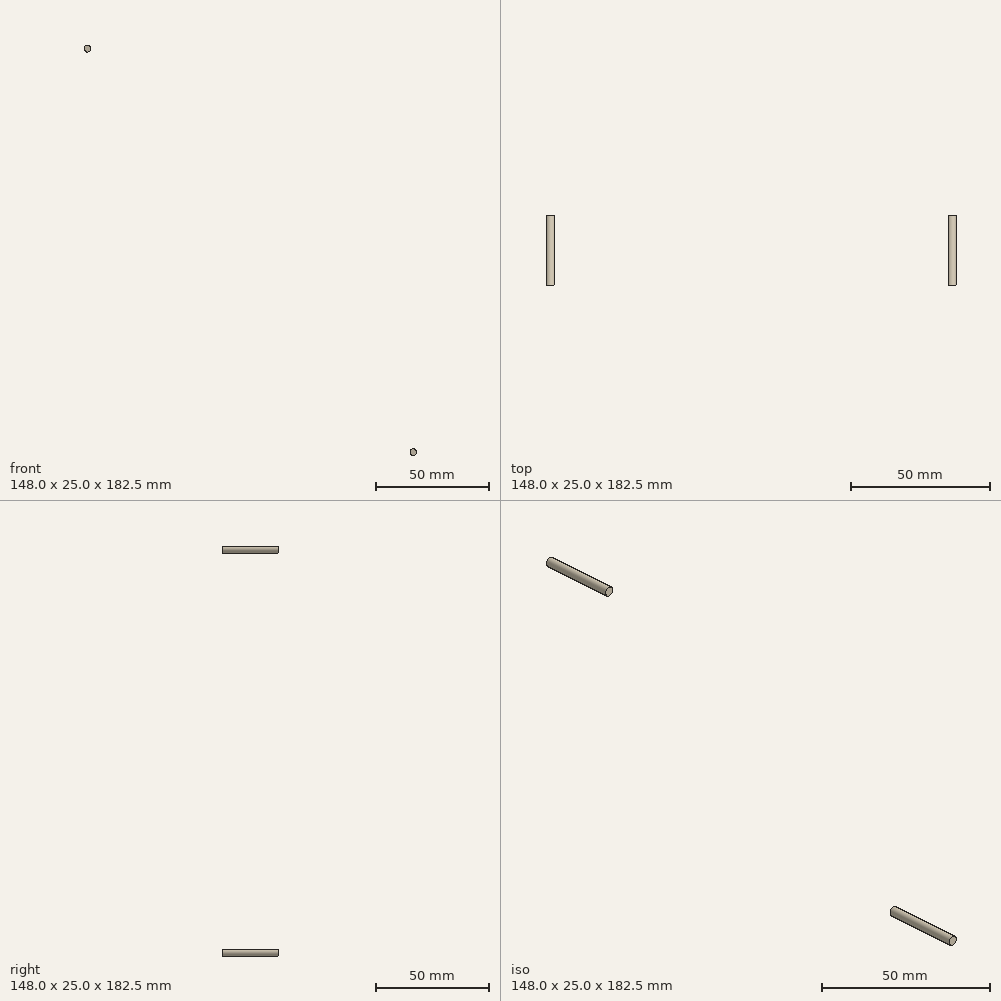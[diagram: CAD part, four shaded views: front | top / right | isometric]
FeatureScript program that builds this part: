
annotation { "Feature Type Name" : "Feature", "Feature Type Description" : "" }
export const myFeature = defineFeature(function(context is Context, id is Id, definition is map)
    precondition{}
    {
        {
            var Q0;
            Q0=qCreatedBy(makeId("Front.planeOp"),FACE);
            var sketch = newSketch(context, id + "F0", { "sketchPlane" : qUnion([Q0])});
            skCircle(sketch, "E0", {"center": v(10, 273.5) * mm, "radius": 1.5 * mm});
            skCircle(sketch, "E1", {"center": v(53, 273.5) * mm, "radius": 1.5 * mm});
            skCircle(sketch, "E2", {"center": v(55, 10) * mm, "radius": 1.5 * mm});
            skCircle(sketch, "E3", {"center": v(145, 10) * mm, "radius": 1.5 * mm});
            skCircle(sketch, "E4", {"center": v(235, 10) * mm, "radius": 1.5 * mm});
            skCircle(sketch, "E5", {"center": v(325, 10) * mm, "radius": 1.5 * mm});
            skCircle(sketch, "E6", {"center": v(345, 364) * mm, "radius": 1.23 * mm});
            skCircle(sketch, "E7", {"center": v(365, 364) * mm, "radius": 1.23 * mm});
            skCircle(sketch, "E8", {"center": v(355, 24) * mm, "radius": 1.23 * mm});
            skCircle(sketch, "E9", {"center": v(345, 44) * mm, "radius": 1.23 * mm});
            skCircle(sketch, "E10", {"center": v(365, 44) * mm, "radius": 1.23 * mm});
            skCircle(sketch, "E11", {"center": v(25, 24) * mm, "radius": 1.23 * mm});
            skCircle(sketch, "E12", {"center": v(15, 44) * mm, "radius": 1.23 * mm});
            skCircle(sketch, "E13", {"center": v(35, 44) * mm, "radius": 1.23 * mm});
            skCircle(sketch, "E14", {"center": v(53, 72) * mm, "radius": 1.23 * mm});
            skCircle(sketch, "E15", {"center": v(10, 72) * mm, "radius": 1.23 * mm});
            skCircle(sketch, "E16", {"center": v(8.74, 104) * mm, "radius": 1.23 * mm});
            skCircle(sketch, "E17", {"center": v(57, 104) * mm, "radius": 1.23 * mm});
            skCircle(sketch, "E18", {"center": v(53, 166) * mm, "radius": 1.23 * mm});
            skCircle(sketch, "E19", {"center": v(10, 166) * mm, "radius": 1.23 * mm});
            skCircle(sketch, "E20", {"center": v(8.74, 185.28) * mm, "radius": 1.23 * mm});
            skCircle(sketch, "E21", {"center": v(57, 178.93) * mm, "radius": 1.23 * mm});
            skCircle(sketch, "E22", {"center": v(35, 364) * mm, "radius": 1.23 * mm});
            skCircle(sketch, "E23", {"center": v(15, 364) * mm, "radius": 1.23 * mm});
            skLineSegment(sketch, "E24", {"start": v(60, 329) * mm, "end": v(65, 334) * mm});
            skLineSegment(sketch, "E25", {"start": v(65, 334) * mm, "end": v(315, 334) * mm});
            skLineSegment(sketch, "E26", {"start": v(315, 334) * mm, "end": v(320, 329) * mm});
            skLineSegment(sketch, "E27", {"start": v(320, 329) * mm, "end": v(320, 59) * mm});
            skLineSegment(sketch, "E28", {"start": v(320, 59) * mm, "end": v(305, 44) * mm});
            skLineSegment(sketch, "E29", {"start": v(285, 44) * mm, "end": v(280, 39) * mm});
            skLineSegment(sketch, "E30", {"start": v(280, 39) * mm, "end": v(280, 24) * mm});
            skArc(sketch, "E31", {"start": v(270, 24) * mm, "mid": v(275, 19) * mm, "end": v(280, 24) * mm});
            skLineSegment(sketch, "E32", {"start": v(270, 24) * mm, "end": v(270, 39) * mm});
            skLineSegment(sketch, "E33", {"start": v(270, 39) * mm, "end": v(265, 44) * mm});
            skLineSegment(sketch, "E34", {"start": v(265, 44) * mm, "end": v(220, 44) * mm});
            skLineSegment(sketch, "E35", {"start": v(220, 44) * mm, "end": v(195, 19) * mm});
            skLineSegment(sketch, "E36", {"start": v(195, 19) * mm, "end": v(185, 19) * mm});
            skLineSegment(sketch, "E37", {"start": v(185, 19) * mm, "end": v(160, 44) * mm});
            skLineSegment(sketch, "E38", {"start": v(160, 44) * mm, "end": v(115, 44) * mm});
            skLineSegment(sketch, "E39", {"start": v(115, 44) * mm, "end": v(110, 39) * mm});
            skLineSegment(sketch, "E40", {"start": v(110, 39) * mm, "end": v(110, 24) * mm});
            skArc(sketch, "E41", {"start": v(100, 24) * mm, "mid": v(105, 19) * mm, "end": v(110, 24) * mm});
            skLineSegment(sketch, "E42", {"start": v(100, 24) * mm, "end": v(100, 39) * mm});
            skLineSegment(sketch, "E43", {"start": v(100, 39) * mm, "end": v(95, 44) * mm});
            skLineSegment(sketch, "E44", {"start": v(65, 54) * mm, "end": v(60, 59) * mm});
            skLineSegment(sketch, "E45", {"start": v(60, 59) * mm, "end": v(60, 329) * mm});
            skCircle(sketch, "E46", {"center": v(25, 14) * mm, "radius": 4 * mm});
            skCircle(sketch, "E47", {"center": v(355, 14) * mm, "radius": 4 * mm});
            skLineSegment(sketch, "E48", {"start": v(344, 10) * mm, "end": v(338, 10) * mm});
            skLineSegment(sketch, "E49", {"start": v(338, 10) * mm, "end": v(334, 6) * mm});
            skLineSegment(sketch, "E50", {"start": v(334, 6) * mm, "end": v(46, 6) * mm});
            skLineSegment(sketch, "E51", {"start": v(46, 6) * mm, "end": v(42, 10) * mm});
            skLineSegment(sketch, "E52", {"start": v(42, 10) * mm, "end": v(36, 10) * mm});
            skLineSegment(sketch, "E53", {"start": v(36, 10) * mm, "end": v(30, 4) * mm});
            skLineSegment(sketch, "E54", {"start": v(30, 4) * mm, "end": v(10, 4) * mm});
            skLineSegment(sketch, "E55", {"start": v(10, 4) * mm, "end": v(5, 8.8) * mm});
            skLineSegment(sketch, "E56", {"start": v(5, 8.8) * mm, "end": v(5, 369) * mm});
            skLineSegment(sketch, "E57", {"start": v(5, 369) * mm, "end": v(10, 374) * mm});
            skLineSegment(sketch, "E58", {"start": v(10, 374) * mm, "end": v(370, 374) * mm});
            skLineSegment(sketch, "E59", {"start": v(370, 374) * mm, "end": v(375, 369) * mm});
            skLineSegment(sketch, "E60", {"start": v(375, 369) * mm, "end": v(375, 9) * mm});
            skLineSegment(sketch, "E61", {"start": v(375, 9) * mm, "end": v(370, 4) * mm});
            skLineSegment(sketch, "E62", {"start": v(370, 4) * mm, "end": v(350, 4) * mm});
            skLineSegment(sketch, "E63", {"start": v(350, 4) * mm, "end": v(344, 10) * mm});
            skCircle(sketch, "E64", {"center": v(155, 94) * mm, "radius": 1.5 * mm});
            skCircle(sketch, "E65", {"center": v(155, 114) * mm, "radius": 1.5 * mm});
            skCircle(sketch, "E66", {"center": v(225, 114) * mm, "radius": 1.5 * mm});
            skCircle(sketch, "E67", {"center": v(225, 94) * mm, "radius": 1.5 * mm});
            skCircle(sketch, "E68", {"center": v(190, 264) * mm, "radius": 1.5 * mm});
            skCircle(sketch, "E69", {"center": v(190, 284) * mm, "radius": 1.5 * mm});
            skCircle(sketch, "E70", {"center": v(85.5, 84.5) * mm, "radius": 1.23 * mm});
            skCircle(sketch, "E71", {"center": v(294.5, 84.5) * mm, "radius": 1.23 * mm});
            skCircle(sketch, "E72", {"center": v(294.5, 293.5) * mm, "radius": 1.23 * mm});
            skCircle(sketch, "E73", {"center": v(211, 189) * mm, "radius": 1.23 * mm});
            skCircle(sketch, "E74", {"center": v(170, 189) * mm, "radius": 1.23 * mm});
            skCircle(sketch, "E75", {"center": v(85.5, 293.5) * mm, "radius": 1.23 * mm});
            skLineSegment(sketch, "E76", {"start": v(265, 121) * mm, "end": v(225, 161) * mm});
            skLineSegment(sketch, "E77", {"start": v(265, 257) * mm, "end": v(265, 121) * mm});
            skLineSegment(sketch, "E78", {"start": v(225, 217) * mm, "end": v(265, 257) * mm});
            skLineSegment(sketch, "E79", {"start": v(225, 161) * mm, "end": v(225, 217) * mm});
            skLineSegment(sketch, "E80", {"start": v(115, 257) * mm, "end": v(155, 217) * mm});
            skLineSegment(sketch, "E81", {"start": v(115, 121) * mm, "end": v(115, 257) * mm});
            skLineSegment(sketch, "E82", {"start": v(155, 161) * mm, "end": v(115, 121) * mm});
            skLineSegment(sketch, "E83", {"start": v(155, 217) * mm, "end": v(155, 161) * mm});
            skLineSegment(sketch, "E84", {"start": v(195, 109) * mm, "end": v(185, 109) * mm});
            skLineSegment(sketch, "E85", {"start": v(215, 129) * mm, "end": v(195, 109) * mm});
            skLineSegment(sketch, "E86", {"start": v(215, 149) * mm, "end": v(215, 129) * mm});
            skLineSegment(sketch, "E87", {"start": v(195, 169) * mm, "end": v(215, 149) * mm});
            skLineSegment(sketch, "E88", {"start": v(185, 169) * mm, "end": v(195, 169) * mm});
            skLineSegment(sketch, "E89", {"start": v(165, 149) * mm, "end": v(185, 169) * mm});
            skLineSegment(sketch, "E90", {"start": v(165, 129) * mm, "end": v(165, 149) * mm});
            skLineSegment(sketch, "E91", {"start": v(185, 109) * mm, "end": v(165, 129) * mm});
            skLineSegment(sketch, "E92", {"start": v(165, 229) * mm, "end": v(165, 239) * mm});
            skLineSegment(sketch, "E93", {"start": v(185, 209) * mm, "end": v(165, 229) * mm});
            skLineSegment(sketch, "E94", {"start": v(195, 209) * mm, "end": v(185, 209) * mm});
            skLineSegment(sketch, "E95", {"start": v(215, 229) * mm, "end": v(195, 209) * mm});
            skLineSegment(sketch, "E96", {"start": v(215, 239) * mm, "end": v(215, 229) * mm});
            skLineSegment(sketch, "E97", {"start": v(195, 259) * mm, "end": v(215, 239) * mm});
            skLineSegment(sketch, "E98", {"start": v(185, 259) * mm, "end": v(195, 259) * mm});
            skLineSegment(sketch, "E99", {"start": v(165, 239) * mm, "end": v(185, 259) * mm});
            skArc(sketch, "E100", {"start": v(236, 99) * mm, "mid": v(238.83, 100.17) * mm, "end": v(240, 103) * mm});
            skLineSegment(sketch, "E101", {"start": v(240, 105) * mm, "end": v(240, 103) * mm});
            skArc(sketch, "E102", {"start": v(240, 105) * mm, "mid": v(238.83, 107.83) * mm, "end": v(236, 109) * mm});
            skLineSegment(sketch, "E103", {"start": v(213, 109) * mm, "end": v(236, 109) * mm});
            skArc(sketch, "E104", {"start": v(213, 109) * mm, "mid": v(210.17, 107.83) * mm, "end": v(209, 105) * mm});
            skLineSegment(sketch, "E105", {"start": v(209, 103) * mm, "end": v(209, 105) * mm});
            skArc(sketch, "E106", {"start": v(209, 103) * mm, "mid": v(210.17, 100.17) * mm, "end": v(213, 99) * mm});
            skLineSegment(sketch, "E107", {"start": v(236, 99) * mm, "end": v(213, 99) * mm});
            skArc(sketch, "E108", {"start": v(202.14, 269) * mm, "mid": v(204.97, 270.17) * mm, "end": v(206.14, 273) * mm});
            skLineSegment(sketch, "E109", {"start": v(206.14, 275) * mm, "end": v(206.14, 273) * mm});
            skArc(sketch, "E110", {"start": v(206.14, 275) * mm, "mid": v(204.97, 277.83) * mm, "end": v(202.14, 279) * mm});
            skLineSegment(sketch, "E111", {"start": v(179.14, 279) * mm, "end": v(202.14, 279) * mm});
            skArc(sketch, "E112", {"start": v(179.14, 279) * mm, "mid": v(176.3, 277.83) * mm, "end": v(175.14, 275) * mm});
            skLineSegment(sketch, "E113", {"start": v(175.14, 273) * mm, "end": v(175.14, 275) * mm});
            skArc(sketch, "E114", {"start": v(175.14, 273) * mm, "mid": v(176.3, 270.17) * mm, "end": v(179.14, 269) * mm});
            skLineSegment(sketch, "E115", {"start": v(202.14, 269) * mm, "end": v(179.14, 269) * mm});
            skArc(sketch, "E116", {"start": v(166, 99) * mm, "mid": v(168.82, 100.17) * mm, "end": v(170, 103) * mm});
            skLineSegment(sketch, "E117", {"start": v(170, 105) * mm, "end": v(170, 103) * mm});
            skArc(sketch, "E118", {"start": v(170, 105) * mm, "mid": v(168.82, 107.83) * mm, "end": v(166, 109) * mm});
            skLineSegment(sketch, "E119", {"start": v(143, 109) * mm, "end": v(166, 109) * mm});
            skArc(sketch, "E120", {"start": v(143, 109) * mm, "mid": v(140.16, 107.83) * mm, "end": v(139, 105) * mm});
            skLineSegment(sketch, "E121", {"start": v(139, 103) * mm, "end": v(139, 105) * mm});
            skArc(sketch, "E122", {"start": v(139, 103) * mm, "mid": v(140.16, 100.17) * mm, "end": v(143, 99) * mm});
            skLineSegment(sketch, "E123", {"start": v(166, 99) * mm, "end": v(143, 99) * mm});
            skLineSegment(sketch, "E124", {"start": v(80, 82) * mm, "end": v(83, 79) * mm});
            skLineSegment(sketch, "E125", {"start": v(83, 79) * mm, "end": v(87, 79) * mm});
            skLineSegment(sketch, "E126", {"start": v(87, 79) * mm, "end": v(107, 99) * mm});
            skLineSegment(sketch, "E127", {"start": v(107, 99) * mm, "end": v(127, 99) * mm});
            skLineSegment(sketch, "E128", {"start": v(127, 99) * mm, "end": v(137, 89) * mm});
            skLineSegment(sketch, "E129", {"start": v(137, 89) * mm, "end": v(175, 89) * mm});
            skLineSegment(sketch, "E130", {"start": v(175, 89) * mm, "end": v(185, 99) * mm});
            skLineSegment(sketch, "E131", {"start": v(185, 99) * mm, "end": v(195, 99) * mm});
            skLineSegment(sketch, "E132", {"start": v(195, 99) * mm, "end": v(205, 89) * mm});
            skLineSegment(sketch, "E133", {"start": v(205, 89) * mm, "end": v(243, 89) * mm});
            skLineSegment(sketch, "E134", {"start": v(243, 89) * mm, "end": v(253, 99) * mm});
            skLineSegment(sketch, "E135", {"start": v(253, 99) * mm, "end": v(273, 99) * mm});
            skLineSegment(sketch, "E136", {"start": v(273, 99) * mm, "end": v(293, 79) * mm});
            skLineSegment(sketch, "E137", {"start": v(293, 79) * mm, "end": v(297, 79) * mm});
            skLineSegment(sketch, "E138", {"start": v(297, 79) * mm, "end": v(300, 82) * mm});
            skLineSegment(sketch, "E139", {"start": v(300, 82) * mm, "end": v(300, 86) * mm});
            skLineSegment(sketch, "E140", {"start": v(300, 86) * mm, "end": v(275, 111) * mm});
            skLineSegment(sketch, "E141", {"start": v(275, 111) * mm, "end": v(275, 267) * mm});
            skLineSegment(sketch, "E142", {"start": v(275, 267) * mm, "end": v(300, 292) * mm});
            skLineSegment(sketch, "E143", {"start": v(300, 292) * mm, "end": v(300, 296) * mm});
            skLineSegment(sketch, "E144", {"start": v(300, 296) * mm, "end": v(297, 299) * mm});
            skLineSegment(sketch, "E145", {"start": v(297, 299) * mm, "end": v(293, 299) * mm});
            skLineSegment(sketch, "E146", {"start": v(293, 299) * mm, "end": v(253, 259) * mm});
            skLineSegment(sketch, "E147", {"start": v(253, 259) * mm, "end": v(233, 259) * mm});
            skLineSegment(sketch, "E148", {"start": v(233, 259) * mm, "end": v(203, 289) * mm});
            skLineSegment(sketch, "E149", {"start": v(203, 289) * mm, "end": v(177, 289) * mm});
            skLineSegment(sketch, "E150", {"start": v(177, 289) * mm, "end": v(147, 259) * mm});
            skLineSegment(sketch, "E151", {"start": v(147, 259) * mm, "end": v(127, 259) * mm});
            skLineSegment(sketch, "E152", {"start": v(127, 259) * mm, "end": v(87, 299) * mm});
            skLineSegment(sketch, "E153", {"start": v(87, 299) * mm, "end": v(83, 299) * mm});
            skLineSegment(sketch, "E154", {"start": v(83, 299) * mm, "end": v(80, 296) * mm});
            skLineSegment(sketch, "E155", {"start": v(80, 296) * mm, "end": v(80, 292) * mm});
            skLineSegment(sketch, "E156", {"start": v(80, 292) * mm, "end": v(105, 267) * mm});
            skLineSegment(sketch, "E157", {"start": v(105, 267) * mm, "end": v(105, 111) * mm});
            skLineSegment(sketch, "E158", {"start": v(105, 111) * mm, "end": v(80, 86) * mm});
            skLineSegment(sketch, "E159", {"start": v(80, 86) * mm, "end": v(80, 82) * mm});
            skLineSegment(sketch, "E160", {"start": v(279.72, 358.5) * mm, "end": v(279.72, 341.5) * mm});
            skLineSegment(sketch, "E161", {"start": v(279.72, 341.5) * mm, "end": v(273.9, 341.5) * mm});
            skLineSegment(sketch, "E162", {"start": v(273.9, 341.5) * mm, "end": v(273.9, 358.5) * mm});
            skLineSegment(sketch, "E163", {"start": v(68.6, 362.17) * mm, "end": v(68.6, 341.5) * mm});
            skLineSegment(sketch, "E164", {"start": v(68.6, 341.5) * mm, "end": v(62.89, 341.5) * mm});
            skLineSegment(sketch, "E165", {"start": v(62.89, 341.5) * mm, "end": v(62.89, 366.5) * mm});
            skLineSegment(sketch, "E166", {"start": v(62.89, 366.5) * mm, "end": v(84.27, 366.5) * mm});
            skLineSegment(sketch, "E167", {"start": v(84.27, 366.5) * mm, "end": v(84.76, 366.5) * mm});
            skLineSegment(sketch, "E168", {"start": v(84.76, 366.5) * mm, "end": v(85.22, 366.47) * mm});
            skLineSegment(sketch, "E169", {"start": v(85.22, 366.47) * mm, "end": v(85.66, 366.43) * mm});
            skLineSegment(sketch, "E170", {"start": v(85.66, 366.43) * mm, "end": v(86.07, 366.37) * mm});
            skLineSegment(sketch, "E171", {"start": v(86.07, 366.37) * mm, "end": v(86.46, 366.3) * mm});
            skLineSegment(sketch, "E172", {"start": v(86.46, 366.3) * mm, "end": v(86.83, 366.21) * mm});
            skLineSegment(sketch, "E173", {"start": v(86.83, 366.21) * mm, "end": v(87.18, 366.1) * mm});
            skLineSegment(sketch, "E174", {"start": v(87.18, 366.1) * mm, "end": v(87.5, 365.99) * mm});
            skLineSegment(sketch, "E175", {"start": v(87.5, 365.99) * mm, "end": v(87.8, 365.85) * mm});
            skLineSegment(sketch, "E176", {"start": v(87.8, 365.85) * mm, "end": v(88.09, 365.7) * mm});
            skLineSegment(sketch, "E177", {"start": v(88.09, 365.7) * mm, "end": v(88.35, 365.53) * mm});
            skLineSegment(sketch, "E178", {"start": v(88.35, 365.53) * mm, "end": v(88.58, 365.35) * mm});
            skLineSegment(sketch, "E179", {"start": v(88.58, 365.35) * mm, "end": v(88.8, 365.15) * mm});
            skLineSegment(sketch, "E180", {"start": v(88.8, 365.15) * mm, "end": v(88.99, 364.93) * mm});
            skLineSegment(sketch, "E181", {"start": v(88.99, 364.93) * mm, "end": v(89.16, 364.69) * mm});
            skLineSegment(sketch, "E182", {"start": v(89.16, 364.69) * mm, "end": v(89.32, 364.43) * mm});
            skLineSegment(sketch, "E183", {"start": v(89.32, 364.43) * mm, "end": v(89.46, 364.15) * mm});
            skLineSegment(sketch, "E184", {"start": v(89.46, 364.15) * mm, "end": v(89.58, 363.85) * mm});
            skLineSegment(sketch, "E185", {"start": v(89.58, 363.85) * mm, "end": v(89.68, 363.53) * mm});
            skLineSegment(sketch, "E186", {"start": v(89.68, 363.53) * mm, "end": v(89.77, 363.2) * mm});
            skLineSegment(sketch, "E187", {"start": v(89.77, 363.2) * mm, "end": v(89.83, 362.84) * mm});
            skLineSegment(sketch, "E188", {"start": v(89.83, 362.84) * mm, "end": v(89.88, 362.46) * mm});
            skLineSegment(sketch, "E189", {"start": v(89.88, 362.46) * mm, "end": v(89.9, 362.06) * mm});
            skLineSegment(sketch, "E190", {"start": v(89.9, 362.06) * mm, "end": v(89.92, 361.65) * mm});
            skLineSegment(sketch, "E191", {"start": v(89.92, 361.65) * mm, "end": v(89.92, 356.08) * mm});
            skLineSegment(sketch, "E192", {"start": v(89.92, 356.08) * mm, "end": v(89.9, 355.67) * mm});
            skLineSegment(sketch, "E193", {"start": v(89.9, 355.67) * mm, "end": v(89.88, 355.28) * mm});
            skLineSegment(sketch, "E194", {"start": v(89.88, 355.28) * mm, "end": v(89.83, 354.9) * mm});
            skLineSegment(sketch, "E195", {"start": v(89.83, 354.9) * mm, "end": v(89.77, 354.55) * mm});
            skLineSegment(sketch, "E196", {"start": v(89.77, 354.55) * mm, "end": v(89.68, 354.21) * mm});
            skLineSegment(sketch, "E197", {"start": v(89.68, 354.21) * mm, "end": v(89.58, 353.9) * mm});
            skLineSegment(sketch, "E198", {"start": v(89.58, 353.9) * mm, "end": v(89.46, 353.6) * mm});
            skLineSegment(sketch, "E199", {"start": v(89.46, 353.6) * mm, "end": v(89.32, 353.32) * mm});
            skLineSegment(sketch, "E200", {"start": v(89.32, 353.32) * mm, "end": v(89.16, 353.06) * mm});
            skLineSegment(sketch, "E201", {"start": v(89.16, 353.06) * mm, "end": v(88.99, 352.83) * mm});
            skLineSegment(sketch, "E202", {"start": v(88.99, 352.83) * mm, "end": v(88.8, 352.6) * mm});
            skLineSegment(sketch, "E203", {"start": v(88.8, 352.6) * mm, "end": v(88.58, 352.4) * mm});
            skLineSegment(sketch, "E204", {"start": v(88.58, 352.4) * mm, "end": v(88.35, 352.22) * mm});
            skLineSegment(sketch, "E205", {"start": v(88.35, 352.22) * mm, "end": v(88.09, 352.05) * mm});
            skLineSegment(sketch, "E206", {"start": v(88.09, 352.05) * mm, "end": v(87.8, 351.9) * mm});
            skLineSegment(sketch, "E207", {"start": v(87.8, 351.9) * mm, "end": v(87.5, 351.76) * mm});
            skLineSegment(sketch, "E208", {"start": v(87.5, 351.76) * mm, "end": v(87.18, 351.64) * mm});
            skLineSegment(sketch, "E209", {"start": v(87.18, 351.64) * mm, "end": v(86.83, 351.54) * mm});
            skLineSegment(sketch, "E210", {"start": v(86.83, 351.54) * mm, "end": v(86.46, 351.45) * mm});
            skLineSegment(sketch, "E211", {"start": v(86.46, 351.45) * mm, "end": v(86.07, 351.38) * mm});
            skLineSegment(sketch, "E212", {"start": v(86.07, 351.38) * mm, "end": v(85.66, 351.32) * mm});
            skLineSegment(sketch, "E213", {"start": v(85.66, 351.32) * mm, "end": v(85.22, 351.28) * mm});
            skLineSegment(sketch, "E214", {"start": v(85.22, 351.28) * mm, "end": v(84.76, 351.26) * mm});
            skLineSegment(sketch, "E215", {"start": v(84.76, 351.26) * mm, "end": v(84.27, 351.25) * mm});
            skLineSegment(sketch, "E216", {"start": v(84.27, 351.25) * mm, "end": v(71.25, 351.25) * mm});
            skLineSegment(sketch, "E217", {"start": v(71.25, 355.56) * mm, "end": v(81.7, 355.56) * mm});
            skLineSegment(sketch, "E218", {"start": v(81.7, 355.56) * mm, "end": v(81.94, 355.56) * mm});
            skLineSegment(sketch, "E219", {"start": v(81.94, 355.56) * mm, "end": v(82.17, 355.57) * mm});
            skLineSegment(sketch, "E220", {"start": v(82.17, 355.57) * mm, "end": v(82.4, 355.59) * mm});
            skLineSegment(sketch, "E221", {"start": v(82.4, 355.59) * mm, "end": v(82.6, 355.6) * mm});
            skLineSegment(sketch, "E222", {"start": v(82.6, 355.6) * mm, "end": v(82.8, 355.63) * mm});
            skLineSegment(sketch, "E223", {"start": v(82.8, 355.63) * mm, "end": v(82.97, 355.67) * mm});
            skLineSegment(sketch, "E224", {"start": v(82.97, 355.67) * mm, "end": v(83.14, 355.7) * mm});
            skLineSegment(sketch, "E225", {"start": v(83.14, 355.7) * mm, "end": v(83.29, 355.75) * mm});
            skLineSegment(sketch, "E226", {"start": v(83.29, 355.75) * mm, "end": v(83.43, 355.8) * mm});
            skLineSegment(sketch, "E227", {"start": v(83.43, 355.8) * mm, "end": v(83.55, 355.86) * mm});
            skLineSegment(sketch, "E228", {"start": v(83.55, 355.86) * mm, "end": v(83.67, 355.92) * mm});
            skLineSegment(sketch, "E229", {"start": v(83.67, 355.92) * mm, "end": v(83.76, 356) * mm});
            skLineSegment(sketch, "E230", {"start": v(83.76, 356) * mm, "end": v(83.85, 356.07) * mm});
            skLineSegment(sketch, "E231", {"start": v(83.85, 356.07) * mm, "end": v(83.94, 356.16) * mm});
            skLineSegment(sketch, "E232", {"start": v(83.94, 356.16) * mm, "end": v(84, 356.25) * mm});
            skLineSegment(sketch, "E233", {"start": v(84, 356.25) * mm, "end": v(84.07, 356.36) * mm});
            skLineSegment(sketch, "E234", {"start": v(84.07, 356.36) * mm, "end": v(84.13, 356.47) * mm});
            skLineSegment(sketch, "E235", {"start": v(84.13, 356.47) * mm, "end": v(84.18, 356.6) * mm});
            skLineSegment(sketch, "E236", {"start": v(84.18, 356.6) * mm, "end": v(84.23, 356.73) * mm});
            skLineSegment(sketch, "E237", {"start": v(84.23, 356.73) * mm, "end": v(84.26, 356.87) * mm});
            skLineSegment(sketch, "E238", {"start": v(84.26, 356.87) * mm, "end": v(84.29, 357.03) * mm});
            skLineSegment(sketch, "E239", {"start": v(84.29, 357.03) * mm, "end": v(84.3, 357.19) * mm});
            skLineSegment(sketch, "E240", {"start": v(84.3, 357.19) * mm, "end": v(84.32, 357.36) * mm});
            skLineSegment(sketch, "E241", {"start": v(84.32, 357.36) * mm, "end": v(84.32, 357.54) * mm});
            skLineSegment(sketch, "E242", {"start": v(84.32, 357.54) * mm, "end": v(84.32, 360.21) * mm});
            skLineSegment(sketch, "E243", {"start": v(84.32, 360.21) * mm, "end": v(84.32, 360.39) * mm});
            skLineSegment(sketch, "E244", {"start": v(84.32, 360.39) * mm, "end": v(84.3, 360.56) * mm});
            skLineSegment(sketch, "E245", {"start": v(84.3, 360.56) * mm, "end": v(84.29, 360.72) * mm});
            skLineSegment(sketch, "E246", {"start": v(84.29, 360.72) * mm, "end": v(84.26, 360.87) * mm});
            skLineSegment(sketch, "E247", {"start": v(84.26, 360.87) * mm, "end": v(84.23, 361) * mm});
            skLineSegment(sketch, "E248", {"start": v(84.23, 361) * mm, "end": v(84.18, 361.14) * mm});
            skLineSegment(sketch, "E249", {"start": v(84.18, 361.14) * mm, "end": v(84.13, 361.26) * mm});
            skLineSegment(sketch, "E250", {"start": v(84.13, 361.26) * mm, "end": v(84.07, 361.37) * mm});
            skLineSegment(sketch, "E251", {"start": v(84.07, 361.37) * mm, "end": v(84, 361.48) * mm});
            skLineSegment(sketch, "E252", {"start": v(84, 361.48) * mm, "end": v(83.94, 361.57) * mm});
            skLineSegment(sketch, "E253", {"start": v(83.94, 361.57) * mm, "end": v(83.85, 361.66) * mm});
            skLineSegment(sketch, "E254", {"start": v(83.85, 361.66) * mm, "end": v(83.76, 361.74) * mm});
            skLineSegment(sketch, "E255", {"start": v(83.76, 361.74) * mm, "end": v(83.67, 361.8) * mm});
            skLineSegment(sketch, "E256", {"start": v(83.67, 361.8) * mm, "end": v(83.55, 361.87) * mm});
            skLineSegment(sketch, "E257", {"start": v(83.55, 361.87) * mm, "end": v(83.43, 361.92) * mm});
            skLineSegment(sketch, "E258", {"start": v(83.43, 361.92) * mm, "end": v(83.29, 361.98) * mm});
            skLineSegment(sketch, "E259", {"start": v(83.29, 361.98) * mm, "end": v(83.14, 362.02) * mm});
            skLineSegment(sketch, "E260", {"start": v(83.14, 362.02) * mm, "end": v(82.97, 362.06) * mm});
            skLineSegment(sketch, "E261", {"start": v(82.97, 362.06) * mm, "end": v(82.8, 362.1) * mm});
            skLineSegment(sketch, "E262", {"start": v(82.8, 362.1) * mm, "end": v(82.6, 362.12) * mm});
            skLineSegment(sketch, "E263", {"start": v(82.6, 362.12) * mm, "end": v(82.4, 362.14) * mm});
            skLineSegment(sketch, "E264", {"start": v(82.4, 362.14) * mm, "end": v(82.17, 362.16) * mm});
            skLineSegment(sketch, "E265", {"start": v(82.17, 362.16) * mm, "end": v(81.94, 362.17) * mm});
            skLineSegment(sketch, "E266", {"start": v(81.94, 362.17) * mm, "end": v(81.7, 362.17) * mm});
            skLineSegment(sketch, "E267", {"start": v(81.7, 362.17) * mm, "end": v(68.6, 362.17) * mm});
            skLineSegment(sketch, "E268", {"start": v(311.67, 341.5) * mm, "end": v(297.14, 341.5) * mm});
            skLineSegment(sketch, "E269", {"start": v(297.14, 341.5) * mm, "end": v(296.6, 341.5) * mm});
            skLineSegment(sketch, "E270", {"start": v(296.6, 341.5) * mm, "end": v(296.08, 341.53) * mm});
            skLineSegment(sketch, "E271", {"start": v(296.08, 341.53) * mm, "end": v(295.6, 341.56) * mm});
            skLineSegment(sketch, "E272", {"start": v(295.6, 341.56) * mm, "end": v(295.14, 341.62) * mm});
            skLineSegment(sketch, "E273", {"start": v(295.14, 341.62) * mm, "end": v(294.72, 341.68) * mm});
            skLineSegment(sketch, "E274", {"start": v(294.72, 341.68) * mm, "end": v(294.32, 341.76) * mm});
            skLineSegment(sketch, "E275", {"start": v(294.32, 341.76) * mm, "end": v(293.96, 341.85) * mm});
            skLineSegment(sketch, "E276", {"start": v(293.96, 341.85) * mm, "end": v(293.63, 341.96) * mm});
            skLineSegment(sketch, "E277", {"start": v(293.63, 341.96) * mm, "end": v(293.33, 342.08) * mm});
            skLineSegment(sketch, "E278", {"start": v(293.33, 342.08) * mm, "end": v(293.05, 342.22) * mm});
            skLineSegment(sketch, "E279", {"start": v(293.05, 342.22) * mm, "end": v(292.81, 342.37) * mm});
            skLineSegment(sketch, "E280", {"start": v(292.81, 342.37) * mm, "end": v(292.6, 342.54) * mm});
            skLineSegment(sketch, "E281", {"start": v(292.6, 342.54) * mm, "end": v(292.41, 342.73) * mm});
            skLineSegment(sketch, "E282", {"start": v(292.41, 342.73) * mm, "end": v(292.24, 342.93) * mm});
            skLineSegment(sketch, "E283", {"start": v(292.24, 342.93) * mm, "end": v(292.09, 343.17) * mm});
            skLineSegment(sketch, "E284", {"start": v(292.09, 343.17) * mm, "end": v(291.95, 343.43) * mm});
            skLineSegment(sketch, "E285", {"start": v(291.95, 343.43) * mm, "end": v(291.83, 343.71) * mm});
            skLineSegment(sketch, "E286", {"start": v(291.83, 343.71) * mm, "end": v(291.72, 344.02) * mm});
            skLineSegment(sketch, "E287", {"start": v(291.72, 344.02) * mm, "end": v(291.63, 344.35) * mm});
            skLineSegment(sketch, "E288", {"start": v(291.63, 344.35) * mm, "end": v(291.56, 344.7) * mm});
            skLineSegment(sketch, "E289", {"start": v(291.56, 344.7) * mm, "end": v(291.5, 345.09) * mm});
            skLineSegment(sketch, "E290", {"start": v(291.5, 345.09) * mm, "end": v(291.46, 345.5) * mm});
            skLineSegment(sketch, "E291", {"start": v(291.46, 345.5) * mm, "end": v(291.43, 345.92) * mm});
            skLineSegment(sketch, "E292", {"start": v(291.43, 345.92) * mm, "end": v(291.43, 346.38) * mm});
            skLineSegment(sketch, "E293", {"start": v(291.43, 346.38) * mm, "end": v(291.43, 348.43) * mm});
            skLineSegment(sketch, "E294", {"start": v(291.43, 348.43) * mm, "end": v(296.55, 349.5) * mm});
            skLineSegment(sketch, "E295", {"start": v(296.55, 349.5) * mm, "end": v(296.55, 345.98) * mm});
            skLineSegment(sketch, "E296", {"start": v(296.55, 345.98) * mm, "end": v(310.04, 345.98) * mm});
            skLineSegment(sketch, "E297", {"start": v(310.04, 345.98) * mm, "end": v(310.27, 345.98) * mm});
            skLineSegment(sketch, "E298", {"start": v(310.27, 345.98) * mm, "end": v(310.5, 346) * mm});
            skLineSegment(sketch, "E299", {"start": v(310.5, 346) * mm, "end": v(310.7, 346) * mm});
            skLineSegment(sketch, "E300", {"start": v(310.7, 346) * mm, "end": v(310.9, 346.03) * mm});
            skLineSegment(sketch, "E301", {"start": v(310.9, 346.03) * mm, "end": v(311.07, 346.06) * mm});
            skLineSegment(sketch, "E302", {"start": v(311.07, 346.06) * mm, "end": v(311.24, 346.1) * mm});
            skLineSegment(sketch, "E303", {"start": v(311.24, 346.1) * mm, "end": v(311.4, 346.13) * mm});
            skLineSegment(sketch, "E304", {"start": v(311.4, 346.13) * mm, "end": v(311.53, 346.18) * mm});
            skLineSegment(sketch, "E305", {"start": v(311.53, 346.18) * mm, "end": v(311.66, 346.23) * mm});
            skLineSegment(sketch, "E306", {"start": v(311.66, 346.23) * mm, "end": v(311.77, 346.29) * mm});
            skLineSegment(sketch, "E307", {"start": v(311.77, 346.29) * mm, "end": v(311.87, 346.35) * mm});
            skLineSegment(sketch, "E308", {"start": v(311.87, 346.35) * mm, "end": v(311.96, 346.43) * mm});
            skLineSegment(sketch, "E309", {"start": v(311.96, 346.43) * mm, "end": v(312.04, 346.5) * mm});
            skLineSegment(sketch, "E310", {"start": v(312.04, 346.5) * mm, "end": v(312.1, 346.6) * mm});
            skLineSegment(sketch, "E311", {"start": v(312.1, 346.6) * mm, "end": v(312.17, 346.7) * mm});
            skLineSegment(sketch, "E312", {"start": v(312.17, 346.7) * mm, "end": v(312.23, 346.82) * mm});
            skLineSegment(sketch, "E313", {"start": v(312.23, 346.82) * mm, "end": v(312.28, 346.96) * mm});
            skLineSegment(sketch, "E314", {"start": v(312.28, 346.96) * mm, "end": v(312.32, 347.1) * mm});
            skLineSegment(sketch, "E315", {"start": v(312.32, 347.1) * mm, "end": v(312.36, 347.26) * mm});
            skLineSegment(sketch, "E316", {"start": v(312.36, 347.26) * mm, "end": v(312.39, 347.43) * mm});
            skLineSegment(sketch, "E317", {"start": v(312.39, 347.43) * mm, "end": v(312.41, 347.6) * mm});
            skLineSegment(sketch, "E318", {"start": v(312.41, 347.6) * mm, "end": v(312.43, 347.8) * mm});
            skLineSegment(sketch, "E319", {"start": v(312.43, 347.8) * mm, "end": v(312.44, 348.01) * mm});
            skLineSegment(sketch, "E320", {"start": v(312.44, 348.01) * mm, "end": v(312.44, 348.23) * mm});
            skLineSegment(sketch, "E321", {"start": v(312.44, 348.23) * mm, "end": v(312.44, 350.06) * mm});
            skLineSegment(sketch, "E322", {"start": v(312.44, 350.06) * mm, "end": v(312.44, 350.29) * mm});
            skLineSegment(sketch, "E323", {"start": v(312.44, 350.29) * mm, "end": v(312.43, 350.5) * mm});
            skLineSegment(sketch, "E324", {"start": v(312.43, 350.5) * mm, "end": v(312.4, 350.7) * mm});
            skLineSegment(sketch, "E325", {"start": v(312.4, 350.7) * mm, "end": v(312.39, 350.89) * mm});
            skLineSegment(sketch, "E326", {"start": v(312.39, 350.89) * mm, "end": v(312.35, 351.06) * mm});
            skLineSegment(sketch, "E327", {"start": v(312.35, 351.06) * mm, "end": v(312.32, 351.22) * mm});
            skLineSegment(sketch, "E328", {"start": v(312.32, 351.22) * mm, "end": v(312.27, 351.37) * mm});
            skLineSegment(sketch, "E329", {"start": v(312.27, 351.37) * mm, "end": v(312.22, 351.5) * mm});
            skLineSegment(sketch, "E330", {"start": v(312.22, 351.5) * mm, "end": v(312.16, 351.62) * mm});
            skLineSegment(sketch, "E331", {"start": v(312.16, 351.62) * mm, "end": v(312.1, 351.73) * mm});
            skLineSegment(sketch, "E332", {"start": v(312.1, 351.73) * mm, "end": v(312.02, 351.83) * mm});
            skLineSegment(sketch, "E333", {"start": v(312.02, 351.83) * mm, "end": v(311.95, 351.9) * mm});
            skLineSegment(sketch, "E334", {"start": v(311.95, 351.9) * mm, "end": v(311.86, 351.98) * mm});
            skLineSegment(sketch, "E335", {"start": v(311.86, 351.98) * mm, "end": v(311.76, 352.05) * mm});
            skLineSegment(sketch, "E336", {"start": v(311.76, 352.05) * mm, "end": v(311.64, 352.1) * mm});
            skLineSegment(sketch, "E337", {"start": v(311.64, 352.1) * mm, "end": v(311.51, 352.16) * mm});
            skLineSegment(sketch, "E338", {"start": v(311.51, 352.16) * mm, "end": v(311.37, 352.21) * mm});
            skLineSegment(sketch, "E339", {"start": v(311.37, 352.21) * mm, "end": v(311.22, 352.25) * mm});
            skLineSegment(sketch, "E340", {"start": v(311.22, 352.25) * mm, "end": v(311.06, 352.29) * mm});
            skLineSegment(sketch, "E341", {"start": v(311.06, 352.29) * mm, "end": v(310.88, 352.32) * mm});
            skLineSegment(sketch, "E342", {"start": v(310.88, 352.32) * mm, "end": v(310.69, 352.34) * mm});
            skLineSegment(sketch, "E343", {"start": v(310.69, 352.34) * mm, "end": v(310.48, 352.35) * mm});
            skLineSegment(sketch, "E344", {"start": v(310.48, 352.35) * mm, "end": v(310.27, 352.36) * mm});
            skLineSegment(sketch, "E345", {"start": v(310.27, 352.36) * mm, "end": v(310.04, 352.37) * mm});
            skLineSegment(sketch, "E346", {"start": v(310.04, 352.37) * mm, "end": v(301.6, 352.37) * mm});
            skLineSegment(sketch, "E347", {"start": v(301.6, 352.37) * mm, "end": v(301.6, 356.43) * mm});
            skLineSegment(sketch, "E348", {"start": v(301.6, 356.43) * mm, "end": v(309.12, 356.43) * mm});
            skLineSegment(sketch, "E349", {"start": v(309.12, 356.43) * mm, "end": v(309.35, 356.43) * mm});
            skLineSegment(sketch, "E350", {"start": v(309.35, 356.43) * mm, "end": v(309.57, 356.44) * mm});
            skLineSegment(sketch, "E351", {"start": v(309.57, 356.44) * mm, "end": v(309.77, 356.45) * mm});
            skLineSegment(sketch, "E352", {"start": v(309.77, 356.45) * mm, "end": v(309.96, 356.48) * mm});
            skLineSegment(sketch, "E353", {"start": v(309.96, 356.48) * mm, "end": v(310.14, 356.5) * mm});
            skLineSegment(sketch, "E354", {"start": v(310.14, 356.5) * mm, "end": v(310.3, 356.54) * mm});
            skLineSegment(sketch, "E355", {"start": v(310.3, 356.54) * mm, "end": v(310.45, 356.58) * mm});
            skLineSegment(sketch, "E356", {"start": v(310.45, 356.58) * mm, "end": v(310.59, 356.62) * mm});
            skLineSegment(sketch, "E357", {"start": v(310.59, 356.62) * mm, "end": v(310.71, 356.68) * mm});
            skLineSegment(sketch, "E358", {"start": v(310.71, 356.68) * mm, "end": v(310.82, 356.74) * mm});
            skLineSegment(sketch, "E359", {"start": v(310.82, 356.74) * mm, "end": v(310.92, 356.8) * mm});
            skLineSegment(sketch, "E360", {"start": v(310.92, 356.8) * mm, "end": v(311, 356.87) * mm});
            skLineSegment(sketch, "E361", {"start": v(311, 356.87) * mm, "end": v(311.08, 356.95) * mm});
            skLineSegment(sketch, "E362", {"start": v(311.08, 356.95) * mm, "end": v(311.15, 357.05) * mm});
            skLineSegment(sketch, "E363", {"start": v(311.15, 357.05) * mm, "end": v(311.21, 357.15) * mm});
            skLineSegment(sketch, "E364", {"start": v(311.21, 357.15) * mm, "end": v(311.27, 357.27) * mm});
            skLineSegment(sketch, "E365", {"start": v(311.27, 357.27) * mm, "end": v(311.32, 357.4) * mm});
            skLineSegment(sketch, "E366", {"start": v(311.32, 357.4) * mm, "end": v(311.36, 357.55) * mm});
            skLineSegment(sketch, "E367", {"start": v(311.36, 357.55) * mm, "end": v(311.4, 357.71) * mm});
            skLineSegment(sketch, "E368", {"start": v(311.4, 357.71) * mm, "end": v(311.42, 357.88) * mm});
            skLineSegment(sketch, "E369", {"start": v(311.42, 357.88) * mm, "end": v(311.45, 358.07) * mm});
            skLineSegment(sketch, "E370", {"start": v(311.45, 358.07) * mm, "end": v(311.46, 358.27) * mm});
            skLineSegment(sketch, "E371", {"start": v(311.46, 358.27) * mm, "end": v(311.47, 358.48) * mm});
            skLineSegment(sketch, "E372", {"start": v(311.47, 358.48) * mm, "end": v(311.48, 358.7) * mm});
            skLineSegment(sketch, "E373", {"start": v(311.48, 358.7) * mm, "end": v(311.48, 359.94) * mm});
            skLineSegment(sketch, "E374", {"start": v(311.48, 359.94) * mm, "end": v(311.47, 360.17) * mm});
            skLineSegment(sketch, "E375", {"start": v(311.47, 360.17) * mm, "end": v(311.46, 360.38) * mm});
            skLineSegment(sketch, "E376", {"start": v(311.46, 360.38) * mm, "end": v(311.45, 360.59) * mm});
            skLineSegment(sketch, "E377", {"start": v(311.45, 360.59) * mm, "end": v(311.42, 360.77) * mm});
            skLineSegment(sketch, "E378", {"start": v(311.42, 360.77) * mm, "end": v(311.4, 360.95) * mm});
            skLineSegment(sketch, "E379", {"start": v(311.4, 360.95) * mm, "end": v(311.36, 361.11) * mm});
            skLineSegment(sketch, "E380", {"start": v(311.36, 361.11) * mm, "end": v(311.32, 361.26) * mm});
            skLineSegment(sketch, "E381", {"start": v(311.32, 361.26) * mm, "end": v(311.27, 361.4) * mm});
            skLineSegment(sketch, "E382", {"start": v(311.27, 361.4) * mm, "end": v(311.21, 361.51) * mm});
            skLineSegment(sketch, "E383", {"start": v(311.21, 361.51) * mm, "end": v(311.15, 361.62) * mm});
            skLineSegment(sketch, "E384", {"start": v(311.15, 361.62) * mm, "end": v(311.08, 361.72) * mm});
            skLineSegment(sketch, "E385", {"start": v(311.08, 361.72) * mm, "end": v(311, 361.8) * mm});
            skLineSegment(sketch, "E386", {"start": v(311, 361.8) * mm, "end": v(310.92, 361.87) * mm});
            skLineSegment(sketch, "E387", {"start": v(310.92, 361.87) * mm, "end": v(310.82, 361.93) * mm});
            skLineSegment(sketch, "E388", {"start": v(310.82, 361.93) * mm, "end": v(310.71, 362) * mm});
            skLineSegment(sketch, "E389", {"start": v(310.71, 362) * mm, "end": v(310.59, 362.04) * mm});
            skLineSegment(sketch, "E390", {"start": v(310.59, 362.04) * mm, "end": v(310.45, 362.1) * mm});
            skLineSegment(sketch, "E391", {"start": v(310.45, 362.1) * mm, "end": v(310.3, 362.13) * mm});
            skLineSegment(sketch, "E392", {"start": v(310.3, 362.13) * mm, "end": v(310.14, 362.17) * mm});
            skLineSegment(sketch, "E393", {"start": v(310.14, 362.17) * mm, "end": v(309.96, 362.2) * mm});
            skLineSegment(sketch, "E394", {"start": v(309.96, 362.2) * mm, "end": v(309.77, 362.21) * mm});
            skLineSegment(sketch, "E395", {"start": v(309.77, 362.21) * mm, "end": v(309.57, 362.23) * mm});
            skLineSegment(sketch, "E396", {"start": v(309.57, 362.23) * mm, "end": v(309.35, 362.24) * mm});
            skLineSegment(sketch, "E397", {"start": v(309.35, 362.24) * mm, "end": v(309.12, 362.24) * mm});
            skLineSegment(sketch, "E398", {"start": v(309.12, 362.24) * mm, "end": v(296.77, 362.24) * mm});
            skLineSegment(sketch, "E399", {"start": v(296.77, 362.24) * mm, "end": v(296.77, 359.12) * mm});
            skLineSegment(sketch, "E400", {"start": v(296.77, 359.12) * mm, "end": v(291.82, 360.04) * mm});
            skLineSegment(sketch, "E401", {"start": v(291.82, 360.04) * mm, "end": v(291.82, 361.6) * mm});
            skLineSegment(sketch, "E402", {"start": v(291.82, 361.6) * mm, "end": v(291.83, 362.06) * mm});
            skLineSegment(sketch, "E403", {"start": v(291.83, 362.06) * mm, "end": v(291.85, 362.5) * mm});
            skLineSegment(sketch, "E404", {"start": v(291.85, 362.5) * mm, "end": v(291.9, 362.9) * mm});
            skLineSegment(sketch, "E405", {"start": v(291.9, 362.9) * mm, "end": v(291.95, 363.28) * mm});
            skLineSegment(sketch, "E406", {"start": v(291.95, 363.28) * mm, "end": v(292.02, 363.64) * mm});
            skLineSegment(sketch, "E407", {"start": v(292.02, 363.64) * mm, "end": v(292.11, 363.98) * mm});
            skLineSegment(sketch, "E408", {"start": v(292.11, 363.98) * mm, "end": v(292.22, 364.28) * mm});
            skLineSegment(sketch, "E409", {"start": v(292.22, 364.28) * mm, "end": v(292.34, 364.57) * mm});
            skLineSegment(sketch, "E410", {"start": v(292.34, 364.57) * mm, "end": v(292.48, 364.83) * mm});
            skLineSegment(sketch, "E411", {"start": v(292.48, 364.83) * mm, "end": v(292.63, 365.06) * mm});
            skLineSegment(sketch, "E412", {"start": v(292.63, 365.06) * mm, "end": v(292.8, 365.27) * mm});
            skLineSegment(sketch, "E413", {"start": v(292.8, 365.27) * mm, "end": v(292.99, 365.46) * mm});
            skLineSegment(sketch, "E414", {"start": v(292.99, 365.46) * mm, "end": v(293.2, 365.63) * mm});
            skLineSegment(sketch, "E415", {"start": v(293.2, 365.63) * mm, "end": v(293.43, 365.78) * mm});
            skLineSegment(sketch, "E416", {"start": v(293.43, 365.78) * mm, "end": v(293.7, 365.92) * mm});
            skLineSegment(sketch, "E417", {"start": v(293.7, 365.92) * mm, "end": v(294, 366.04) * mm});
            skLineSegment(sketch, "E418", {"start": v(294, 366.04) * mm, "end": v(294.34, 366.15) * mm});
            skLineSegment(sketch, "E419", {"start": v(294.34, 366.15) * mm, "end": v(294.7, 366.24) * mm});
            skLineSegment(sketch, "E420", {"start": v(294.7, 366.24) * mm, "end": v(295.1, 366.32) * mm});
            skLineSegment(sketch, "E421", {"start": v(295.1, 366.32) * mm, "end": v(295.53, 366.38) * mm});
            skLineSegment(sketch, "E422", {"start": v(295.53, 366.38) * mm, "end": v(295.98, 366.44) * mm});
            skLineSegment(sketch, "E423", {"start": v(295.98, 366.44) * mm, "end": v(296.47, 366.47) * mm});
            skLineSegment(sketch, "E424", {"start": v(296.47, 366.47) * mm, "end": v(296.99, 366.5) * mm});
            skLineSegment(sketch, "E425", {"start": v(296.99, 366.5) * mm, "end": v(297.54, 366.5) * mm});
            skLineSegment(sketch, "E426", {"start": v(297.54, 366.5) * mm, "end": v(311.05, 366.5) * mm});
            skLineSegment(sketch, "E427", {"start": v(311.05, 366.5) * mm, "end": v(311.6, 366.5) * mm});
            skLineSegment(sketch, "E428", {"start": v(311.6, 366.5) * mm, "end": v(312.12, 366.47) * mm});
            skLineSegment(sketch, "E429", {"start": v(312.12, 366.47) * mm, "end": v(312.6, 366.44) * mm});
            skLineSegment(sketch, "E430", {"start": v(312.6, 366.44) * mm, "end": v(313.05, 366.38) * mm});
            skLineSegment(sketch, "E431", {"start": v(313.05, 366.38) * mm, "end": v(313.48, 366.32) * mm});
            skLineSegment(sketch, "E432", {"start": v(313.48, 366.32) * mm, "end": v(313.87, 366.24) * mm});
            skLineSegment(sketch, "E433", {"start": v(313.87, 366.24) * mm, "end": v(314.23, 366.15) * mm});
            skLineSegment(sketch, "E434", {"start": v(314.23, 366.15) * mm, "end": v(314.56, 366.04) * mm});
            skLineSegment(sketch, "E435", {"start": v(314.56, 366.04) * mm, "end": v(314.86, 365.92) * mm});
            skLineSegment(sketch, "E436", {"start": v(314.86, 365.92) * mm, "end": v(315.14, 365.78) * mm});
            skLineSegment(sketch, "E437", {"start": v(315.14, 365.78) * mm, "end": v(315.37, 365.63) * mm});
            skLineSegment(sketch, "E438", {"start": v(315.37, 365.63) * mm, "end": v(315.58, 365.46) * mm});
            skLineSegment(sketch, "E439", {"start": v(315.58, 365.46) * mm, "end": v(315.77, 365.27) * mm});
            skLineSegment(sketch, "E440", {"start": v(315.77, 365.27) * mm, "end": v(315.94, 365.06) * mm});
            skLineSegment(sketch, "E441", {"start": v(315.94, 365.06) * mm, "end": v(316.1, 364.83) * mm});
            skLineSegment(sketch, "E442", {"start": v(316.1, 364.83) * mm, "end": v(316.23, 364.57) * mm});
            skLineSegment(sketch, "E443", {"start": v(316.23, 364.57) * mm, "end": v(316.35, 364.28) * mm});
            skLineSegment(sketch, "E444", {"start": v(316.35, 364.28) * mm, "end": v(316.46, 363.98) * mm});
            skLineSegment(sketch, "E445", {"start": v(316.46, 363.98) * mm, "end": v(316.55, 363.64) * mm});
            skLineSegment(sketch, "E446", {"start": v(316.55, 363.64) * mm, "end": v(316.62, 363.28) * mm});
            skLineSegment(sketch, "E447", {"start": v(316.62, 363.28) * mm, "end": v(316.67, 362.9) * mm});
            skLineSegment(sketch, "E448", {"start": v(316.67, 362.9) * mm, "end": v(316.72, 362.5) * mm});
            skLineSegment(sketch, "E449", {"start": v(316.72, 362.5) * mm, "end": v(316.74, 362.06) * mm});
            skLineSegment(sketch, "E450", {"start": v(316.74, 362.06) * mm, "end": v(316.75, 361.6) * mm});
            skLineSegment(sketch, "E451", {"start": v(316.75, 361.6) * mm, "end": v(316.75, 359.35) * mm});
            skLineSegment(sketch, "E452", {"start": v(317.71, 349.5) * mm, "end": v(317.71, 346.87) * mm});
            skLineSegment(sketch, "E453", {"start": v(317.71, 346.87) * mm, "end": v(317.7, 346.37) * mm});
            skLineSegment(sketch, "E454", {"start": v(317.7, 346.37) * mm, "end": v(317.68, 345.9) * mm});
            skLineSegment(sketch, "E455", {"start": v(317.68, 345.9) * mm, "end": v(317.63, 345.46) * mm});
            skLineSegment(sketch, "E456", {"start": v(317.63, 345.46) * mm, "end": v(317.57, 345.04) * mm});
            skLineSegment(sketch, "E457", {"start": v(317.57, 345.04) * mm, "end": v(317.48, 344.65) * mm});
            skLineSegment(sketch, "E458", {"start": v(317.48, 344.65) * mm, "end": v(317.38, 344.28) * mm});
            skLineSegment(sketch, "E459", {"start": v(317.38, 344.28) * mm, "end": v(317.26, 343.94) * mm});
            skLineSegment(sketch, "E460", {"start": v(317.26, 343.94) * mm, "end": v(317.12, 343.63) * mm});
            skLineSegment(sketch, "E461", {"start": v(317.12, 343.63) * mm, "end": v(316.97, 343.35) * mm});
            skLineSegment(sketch, "E462", {"start": v(316.97, 343.35) * mm, "end": v(316.8, 343.09) * mm});
            skLineSegment(sketch, "E463", {"start": v(316.8, 343.09) * mm, "end": v(316.6, 342.86) * mm});
            skLineSegment(sketch, "E464", {"start": v(316.6, 342.86) * mm, "end": v(316.39, 342.65) * mm});
            skLineSegment(sketch, "E465", {"start": v(316.39, 342.65) * mm, "end": v(316.15, 342.47) * mm});
            skLineSegment(sketch, "E466", {"start": v(316.15, 342.47) * mm, "end": v(315.89, 342.3) * mm});
            skLineSegment(sketch, "E467", {"start": v(315.89, 342.3) * mm, "end": v(315.6, 342.15) * mm});
            skLineSegment(sketch, "E468", {"start": v(315.6, 342.15) * mm, "end": v(315.28, 342.01) * mm});
            skLineSegment(sketch, "E469", {"start": v(315.28, 342.01) * mm, "end": v(314.93, 341.9) * mm});
            skLineSegment(sketch, "E470", {"start": v(314.93, 341.9) * mm, "end": v(314.55, 341.79) * mm});
            skLineSegment(sketch, "E471", {"start": v(314.55, 341.79) * mm, "end": v(314.14, 341.7) * mm});
            skLineSegment(sketch, "E472", {"start": v(314.14, 341.7) * mm, "end": v(313.7, 341.63) * mm});
            skLineSegment(sketch, "E473", {"start": v(313.7, 341.63) * mm, "end": v(313.24, 341.57) * mm});
            skLineSegment(sketch, "E474", {"start": v(313.24, 341.57) * mm, "end": v(312.75, 341.53) * mm});
            skLineSegment(sketch, "E475", {"start": v(312.75, 341.53) * mm, "end": v(312.22, 341.5) * mm});
            skLineSegment(sketch, "E476", {"start": v(312.22, 341.5) * mm, "end": v(311.67, 341.5) * mm});
            skLineSegment(sketch, "E477", {"start": v(273.9, 361.5) * mm, "end": v(273.9, 366.5) * mm});
            skLineSegment(sketch, "E478", {"start": v(273.9, 366.5) * mm, "end": v(279.72, 366.5) * mm});
            skLineSegment(sketch, "E479", {"start": v(279.72, 366.5) * mm, "end": v(279.72, 361.5) * mm});
            skLineSegment(sketch, "E480", {"start": v(137.69, 366.5) * mm, "end": v(143.5, 366.5) * mm});
            skLineSegment(sketch, "E481", {"start": v(143.5, 366.5) * mm, "end": v(143.5, 346.2) * mm});
            skLineSegment(sketch, "E482", {"start": v(143.5, 346.2) * mm, "end": v(160.06, 346.2) * mm});
            skLineSegment(sketch, "E483", {"start": v(160.06, 346.2) * mm, "end": v(160.06, 366.5) * mm});
            skLineSegment(sketch, "E484", {"start": v(160.06, 366.5) * mm, "end": v(165.86, 366.5) * mm});
            skLineSegment(sketch, "E485", {"start": v(165.86, 366.5) * mm, "end": v(165.86, 347.42) * mm});
            skLineSegment(sketch, "E486", {"start": v(165.86, 347.42) * mm, "end": v(165.85, 346.86) * mm});
            skLineSegment(sketch, "E487", {"start": v(165.85, 346.86) * mm, "end": v(165.82, 346.33) * mm});
            skLineSegment(sketch, "E488", {"start": v(165.82, 346.33) * mm, "end": v(165.78, 345.83) * mm});
            skLineSegment(sketch, "E489", {"start": v(165.78, 345.83) * mm, "end": v(165.71, 345.37) * mm});
            skLineSegment(sketch, "E490", {"start": v(165.71, 345.37) * mm, "end": v(165.64, 344.93) * mm});
            skLineSegment(sketch, "E491", {"start": v(165.64, 344.93) * mm, "end": v(165.54, 344.53) * mm});
            skLineSegment(sketch, "E492", {"start": v(165.54, 344.53) * mm, "end": v(165.42, 344.15) * mm});
            skLineSegment(sketch, "E493", {"start": v(165.42, 344.15) * mm, "end": v(165.29, 343.8) * mm});
            skLineSegment(sketch, "E494", {"start": v(165.29, 343.8) * mm, "end": v(165.14, 343.5) * mm});
            skLineSegment(sketch, "E495", {"start": v(165.14, 343.5) * mm, "end": v(164.97, 343.21) * mm});
            skLineSegment(sketch, "E496", {"start": v(164.97, 343.21) * mm, "end": v(164.79, 342.96) * mm});
            skLineSegment(sketch, "E497", {"start": v(164.79, 342.96) * mm, "end": v(164.58, 342.74) * mm});
            skLineSegment(sketch, "E498", {"start": v(164.58, 342.74) * mm, "end": v(164.35, 342.54) * mm});
            skLineSegment(sketch, "E499", {"start": v(164.35, 342.54) * mm, "end": v(164.1, 342.36) * mm});
            skLineSegment(sketch, "E500", {"start": v(164.1, 342.36) * mm, "end": v(163.8, 342.2) * mm});
            skLineSegment(sketch, "E501", {"start": v(163.8, 342.2) * mm, "end": v(163.47, 342.05) * mm});
            skLineSegment(sketch, "E502", {"start": v(163.47, 342.05) * mm, "end": v(163.1, 341.92) * mm});
            skLineSegment(sketch, "E503", {"start": v(163.1, 341.92) * mm, "end": v(162.72, 341.8) * mm});
            skLineSegment(sketch, "E504", {"start": v(162.72, 341.8) * mm, "end": v(162.3, 341.71) * mm});
            skLineSegment(sketch, "E505", {"start": v(162.3, 341.71) * mm, "end": v(161.83, 341.64) * mm});
            skLineSegment(sketch, "E506", {"start": v(161.83, 341.64) * mm, "end": v(161.34, 341.58) * mm});
            skLineSegment(sketch, "E507", {"start": v(161.34, 341.58) * mm, "end": v(160.82, 341.53) * mm});
            skLineSegment(sketch, "E508", {"start": v(160.82, 341.53) * mm, "end": v(160.26, 341.5) * mm});
            skLineSegment(sketch, "E509", {"start": v(160.26, 341.5) * mm, "end": v(159.67, 341.5) * mm});
            skLineSegment(sketch, "E510", {"start": v(159.67, 341.5) * mm, "end": v(143.88, 341.5) * mm});
            skLineSegment(sketch, "E511", {"start": v(143.88, 341.5) * mm, "end": v(143.3, 341.5) * mm});
            skLineSegment(sketch, "E512", {"start": v(143.3, 341.5) * mm, "end": v(142.74, 341.53) * mm});
            skLineSegment(sketch, "E513", {"start": v(142.74, 341.53) * mm, "end": v(142.21, 341.58) * mm});
            skLineSegment(sketch, "E514", {"start": v(142.21, 341.58) * mm, "end": v(141.73, 341.64) * mm});
            skLineSegment(sketch, "E515", {"start": v(141.73, 341.64) * mm, "end": v(141.27, 341.71) * mm});
            skLineSegment(sketch, "E516", {"start": v(141.27, 341.71) * mm, "end": v(140.84, 341.8) * mm});
            skLineSegment(sketch, "E517", {"start": v(140.84, 341.8) * mm, "end": v(140.45, 341.92) * mm});
            skLineSegment(sketch, "E518", {"start": v(140.45, 341.92) * mm, "end": v(140.1, 342.05) * mm});
            skLineSegment(sketch, "E519", {"start": v(140.1, 342.05) * mm, "end": v(139.76, 342.2) * mm});
            skLineSegment(sketch, "E520", {"start": v(139.76, 342.2) * mm, "end": v(139.47, 342.36) * mm});
            skLineSegment(sketch, "E521", {"start": v(139.47, 342.36) * mm, "end": v(139.2, 342.54) * mm});
            skLineSegment(sketch, "E522", {"start": v(139.2, 342.54) * mm, "end": v(138.98, 342.74) * mm});
            skLineSegment(sketch, "E523", {"start": v(138.98, 342.74) * mm, "end": v(138.77, 342.96) * mm});
            skLineSegment(sketch, "E524", {"start": v(138.77, 342.96) * mm, "end": v(138.58, 343.21) * mm});
            skLineSegment(sketch, "E525", {"start": v(138.58, 343.21) * mm, "end": v(138.41, 343.5) * mm});
            skLineSegment(sketch, "E526", {"start": v(138.41, 343.5) * mm, "end": v(138.26, 343.8) * mm});
            skLineSegment(sketch, "E527", {"start": v(138.26, 343.8) * mm, "end": v(138.13, 344.15) * mm});
            skLineSegment(sketch, "E528", {"start": v(138.13, 344.15) * mm, "end": v(138, 344.53) * mm});
            skLineSegment(sketch, "E529", {"start": v(138, 344.53) * mm, "end": v(137.91, 344.93) * mm});
            skLineSegment(sketch, "E530", {"start": v(137.91, 344.93) * mm, "end": v(137.83, 345.37) * mm});
            skLineSegment(sketch, "E531", {"start": v(137.83, 345.37) * mm, "end": v(137.77, 345.83) * mm});
            skLineSegment(sketch, "E532", {"start": v(137.77, 345.83) * mm, "end": v(137.72, 346.33) * mm});
            skLineSegment(sketch, "E533", {"start": v(137.72, 346.33) * mm, "end": v(137.7, 346.86) * mm});
            skLineSegment(sketch, "E534", {"start": v(137.7, 346.86) * mm, "end": v(137.69, 347.42) * mm});
            skLineSegment(sketch, "E535", {"start": v(137.69, 347.42) * mm, "end": v(137.69, 366.5) * mm});
            skLineSegment(sketch, "E536", {"start": v(200.29, 359.27) * mm, "end": v(200.29, 362.12) * mm});
            skLineSegment(sketch, "E537", {"start": v(200.29, 362.12) * mm, "end": v(183.93, 362.12) * mm});
            skLineSegment(sketch, "E538", {"start": v(183.93, 362.12) * mm, "end": v(183.93, 356.75) * mm});
            skLineSegment(sketch, "E539", {"start": v(183.93, 356.75) * mm, "end": v(199.5, 356.75) * mm});
            skLineSegment(sketch, "E540", {"start": v(199.5, 356.75) * mm, "end": v(200.1, 356.74) * mm});
            skLineSegment(sketch, "E541", {"start": v(200.1, 356.74) * mm, "end": v(200.66, 356.71) * mm});
            skLineSegment(sketch, "E542", {"start": v(200.66, 356.71) * mm, "end": v(201.19, 356.67) * mm});
            skLineSegment(sketch, "E543", {"start": v(201.19, 356.67) * mm, "end": v(201.69, 356.6) * mm});
            skLineSegment(sketch, "E544", {"start": v(201.69, 356.6) * mm, "end": v(202.15, 356.53) * mm});
            skLineSegment(sketch, "E545", {"start": v(202.15, 356.53) * mm, "end": v(202.58, 356.44) * mm});
            skLineSegment(sketch, "E546", {"start": v(202.58, 356.44) * mm, "end": v(202.98, 356.32) * mm});
            skLineSegment(sketch, "E547", {"start": v(202.98, 356.32) * mm, "end": v(203.35, 356.2) * mm});
            skLineSegment(sketch, "E548", {"start": v(203.35, 356.2) * mm, "end": v(203.68, 356.04) * mm});
            skLineSegment(sketch, "E549", {"start": v(203.68, 356.04) * mm, "end": v(203.97, 355.88) * mm});
            skLineSegment(sketch, "E550", {"start": v(203.97, 355.88) * mm, "end": v(204.24, 355.7) * mm});
            skLineSegment(sketch, "E551", {"start": v(204.24, 355.7) * mm, "end": v(204.47, 355.5) * mm});
            skLineSegment(sketch, "E552", {"start": v(204.47, 355.5) * mm, "end": v(204.68, 355.27) * mm});
            skLineSegment(sketch, "E553", {"start": v(204.68, 355.27) * mm, "end": v(204.86, 355.02) * mm});
            skLineSegment(sketch, "E554", {"start": v(204.86, 355.02) * mm, "end": v(205.03, 354.74) * mm});
            skLineSegment(sketch, "E555", {"start": v(205.03, 354.74) * mm, "end": v(205.19, 354.42) * mm});
            skLineSegment(sketch, "E556", {"start": v(205.19, 354.42) * mm, "end": v(205.32, 354.08) * mm});
            skLineSegment(sketch, "E557", {"start": v(205.32, 354.08) * mm, "end": v(205.44, 353.7) * mm});
            skLineSegment(sketch, "E558", {"start": v(205.44, 353.7) * mm, "end": v(205.53, 353.3) * mm});
            skLineSegment(sketch, "E559", {"start": v(205.53, 353.3) * mm, "end": v(205.61, 352.87) * mm});
            skLineSegment(sketch, "E560", {"start": v(205.61, 352.87) * mm, "end": v(205.68, 352.4) * mm});
            skLineSegment(sketch, "E561", {"start": v(205.68, 352.4) * mm, "end": v(205.72, 351.91) * mm});
            skLineSegment(sketch, "E562", {"start": v(205.72, 351.91) * mm, "end": v(205.75, 351.39) * mm});
            skLineSegment(sketch, "E563", {"start": v(205.75, 351.39) * mm, "end": v(205.76, 350.83) * mm});
            skLineSegment(sketch, "E564", {"start": v(205.76, 350.83) * mm, "end": v(205.76, 347.42) * mm});
            skLineSegment(sketch, "E565", {"start": v(205.76, 347.42) * mm, "end": v(205.75, 346.86) * mm});
            skLineSegment(sketch, "E566", {"start": v(205.75, 346.86) * mm, "end": v(205.72, 346.34) * mm});
            skLineSegment(sketch, "E567", {"start": v(205.72, 346.34) * mm, "end": v(205.68, 345.84) * mm});
            skLineSegment(sketch, "E568", {"start": v(205.68, 345.84) * mm, "end": v(205.61, 345.38) * mm});
            skLineSegment(sketch, "E569", {"start": v(205.61, 345.38) * mm, "end": v(205.53, 344.95) * mm});
            skLineSegment(sketch, "E570", {"start": v(205.53, 344.95) * mm, "end": v(205.44, 344.54) * mm});
            skLineSegment(sketch, "E571", {"start": v(205.44, 344.54) * mm, "end": v(205.32, 344.17) * mm});
            skLineSegment(sketch, "E572", {"start": v(205.32, 344.17) * mm, "end": v(205.19, 343.82) * mm});
            skLineSegment(sketch, "E573", {"start": v(205.19, 343.82) * mm, "end": v(205.03, 343.51) * mm});
            skLineSegment(sketch, "E574", {"start": v(205.03, 343.51) * mm, "end": v(204.86, 343.23) * mm});
            skLineSegment(sketch, "E575", {"start": v(204.86, 343.23) * mm, "end": v(204.68, 342.97) * mm});
            skLineSegment(sketch, "E576", {"start": v(204.68, 342.97) * mm, "end": v(204.47, 342.75) * mm});
            skLineSegment(sketch, "E577", {"start": v(204.47, 342.75) * mm, "end": v(204.24, 342.55) * mm});
            skLineSegment(sketch, "E578", {"start": v(204.24, 342.55) * mm, "end": v(203.97, 342.37) * mm});
            skLineSegment(sketch, "E579", {"start": v(203.97, 342.37) * mm, "end": v(203.68, 342.2) * mm});
            skLineSegment(sketch, "E580", {"start": v(203.68, 342.2) * mm, "end": v(203.35, 342.06) * mm});
            skLineSegment(sketch, "E581", {"start": v(203.35, 342.06) * mm, "end": v(202.98, 341.93) * mm});
            skLineSegment(sketch, "E582", {"start": v(202.98, 341.93) * mm, "end": v(202.58, 341.81) * mm});
            skLineSegment(sketch, "E583", {"start": v(202.58, 341.81) * mm, "end": v(202.15, 341.72) * mm});
            skLineSegment(sketch, "E584", {"start": v(202.15, 341.72) * mm, "end": v(201.69, 341.64) * mm});
            skLineSegment(sketch, "E585", {"start": v(201.69, 341.64) * mm, "end": v(201.19, 341.58) * mm});
            skLineSegment(sketch, "E586", {"start": v(201.19, 341.58) * mm, "end": v(200.66, 341.53) * mm});
            skLineSegment(sketch, "E587", {"start": v(200.66, 341.53) * mm, "end": v(200.1, 341.5) * mm});
            skLineSegment(sketch, "E588", {"start": v(200.1, 341.5) * mm, "end": v(199.5, 341.5) * mm});
            skLineSegment(sketch, "E589", {"start": v(199.5, 341.5) * mm, "end": v(184.07, 341.5) * mm});
            skLineSegment(sketch, "E590", {"start": v(184.07, 341.5) * mm, "end": v(183.48, 341.5) * mm});
            skLineSegment(sketch, "E591", {"start": v(183.48, 341.5) * mm, "end": v(182.92, 341.53) * mm});
            skLineSegment(sketch, "E592", {"start": v(182.92, 341.53) * mm, "end": v(182.4, 341.58) * mm});
            skLineSegment(sketch, "E593", {"start": v(182.4, 341.58) * mm, "end": v(181.9, 341.64) * mm});
            skLineSegment(sketch, "E594", {"start": v(181.9, 341.64) * mm, "end": v(181.43, 341.72) * mm});
            skLineSegment(sketch, "E595", {"start": v(181.43, 341.72) * mm, "end": v(181, 341.81) * mm});
            skLineSegment(sketch, "E596", {"start": v(181, 341.81) * mm, "end": v(180.6, 341.93) * mm});
            skLineSegment(sketch, "E597", {"start": v(180.6, 341.93) * mm, "end": v(180.25, 342.06) * mm});
            skLineSegment(sketch, "E598", {"start": v(180.25, 342.06) * mm, "end": v(179.92, 342.2) * mm});
            skLineSegment(sketch, "E599", {"start": v(179.92, 342.2) * mm, "end": v(179.62, 342.37) * mm});
            skLineSegment(sketch, "E600", {"start": v(179.62, 342.37) * mm, "end": v(179.35, 342.55) * mm});
            skLineSegment(sketch, "E601", {"start": v(179.35, 342.55) * mm, "end": v(179.12, 342.75) * mm});
            skLineSegment(sketch, "E602", {"start": v(179.12, 342.75) * mm, "end": v(178.92, 342.97) * mm});
            skLineSegment(sketch, "E603", {"start": v(178.92, 342.97) * mm, "end": v(178.73, 343.23) * mm});
            skLineSegment(sketch, "E604", {"start": v(178.73, 343.23) * mm, "end": v(178.56, 343.51) * mm});
            skLineSegment(sketch, "E605", {"start": v(178.56, 343.51) * mm, "end": v(178.4, 343.82) * mm});
            skLineSegment(sketch, "E606", {"start": v(178.4, 343.82) * mm, "end": v(178.27, 344.17) * mm});
            skLineSegment(sketch, "E607", {"start": v(178.27, 344.17) * mm, "end": v(178.16, 344.54) * mm});
            skLineSegment(sketch, "E608", {"start": v(178.16, 344.54) * mm, "end": v(178.06, 344.95) * mm});
            skLineSegment(sketch, "E609", {"start": v(178.06, 344.95) * mm, "end": v(177.98, 345.38) * mm});
            skLineSegment(sketch, "E610", {"start": v(177.98, 345.38) * mm, "end": v(177.92, 345.84) * mm});
            skLineSegment(sketch, "E611", {"start": v(177.92, 345.84) * mm, "end": v(177.87, 346.34) * mm});
            skLineSegment(sketch, "E612", {"start": v(177.87, 346.34) * mm, "end": v(177.85, 346.86) * mm});
            skLineSegment(sketch, "E613", {"start": v(177.85, 346.86) * mm, "end": v(177.84, 347.42) * mm});
            skLineSegment(sketch, "E614", {"start": v(177.84, 347.42) * mm, "end": v(177.84, 348.08) * mm});
            skLineSegment(sketch, "E615", {"start": v(177.84, 348.08) * mm, "end": v(182.96, 349.15) * mm});
            skLineSegment(sketch, "E616", {"start": v(182.96, 349.15) * mm, "end": v(182.96, 346.2) * mm});
            skLineSegment(sketch, "E617", {"start": v(182.96, 346.2) * mm, "end": v(200.63, 346.2) * mm});
            skLineSegment(sketch, "E618", {"start": v(200.63, 346.2) * mm, "end": v(200.63, 351.9) * mm});
            skLineSegment(sketch, "E619", {"start": v(200.63, 351.9) * mm, "end": v(185.04, 351.9) * mm});
            skLineSegment(sketch, "E620", {"start": v(185.04, 351.9) * mm, "end": v(184.45, 351.9) * mm});
            skLineSegment(sketch, "E621", {"start": v(184.45, 351.9) * mm, "end": v(183.9, 351.93) * mm});
            skLineSegment(sketch, "E622", {"start": v(183.9, 351.93) * mm, "end": v(183.37, 351.97) * mm});
            skLineSegment(sketch, "E623", {"start": v(183.37, 351.97) * mm, "end": v(182.88, 352.03) * mm});
            skLineSegment(sketch, "E624", {"start": v(182.88, 352.03) * mm, "end": v(182.42, 352.11) * mm});
            skLineSegment(sketch, "E625", {"start": v(182.42, 352.11) * mm, "end": v(182, 352.2) * mm});
            skLineSegment(sketch, "E626", {"start": v(182, 352.2) * mm, "end": v(181.6, 352.32) * mm});
            skLineSegment(sketch, "E627", {"start": v(181.6, 352.32) * mm, "end": v(181.24, 352.45) * mm});
            skLineSegment(sketch, "E628", {"start": v(181.24, 352.45) * mm, "end": v(180.91, 352.6) * mm});
            skLineSegment(sketch, "E629", {"start": v(180.91, 352.6) * mm, "end": v(180.62, 352.76) * mm});
            skLineSegment(sketch, "E630", {"start": v(180.62, 352.76) * mm, "end": v(180.36, 352.95) * mm});
            skLineSegment(sketch, "E631", {"start": v(180.36, 352.95) * mm, "end": v(180.13, 353.15) * mm});
            skLineSegment(sketch, "E632", {"start": v(180.13, 353.15) * mm, "end": v(179.92, 353.37) * mm});
            skLineSegment(sketch, "E633", {"start": v(179.92, 353.37) * mm, "end": v(179.74, 353.62) * mm});
            skLineSegment(sketch, "E634", {"start": v(179.74, 353.62) * mm, "end": v(179.57, 353.9) * mm});
            skLineSegment(sketch, "E635", {"start": v(179.57, 353.9) * mm, "end": v(179.42, 354.22) * mm});
            skLineSegment(sketch, "E636", {"start": v(179.42, 354.22) * mm, "end": v(179.29, 354.56) * mm});
            skLineSegment(sketch, "E637", {"start": v(179.29, 354.56) * mm, "end": v(179.17, 354.94) * mm});
            skLineSegment(sketch, "E638", {"start": v(179.17, 354.94) * mm, "end": v(179.07, 355.34) * mm});
            skLineSegment(sketch, "E639", {"start": v(179.07, 355.34) * mm, "end": v(179, 355.78) * mm});
            skLineSegment(sketch, "E640", {"start": v(179, 355.78) * mm, "end": v(178.93, 356.24) * mm});
            skLineSegment(sketch, "E641", {"start": v(178.93, 356.24) * mm, "end": v(178.89, 356.73) * mm});
            skLineSegment(sketch, "E642", {"start": v(178.89, 356.73) * mm, "end": v(178.86, 357.26) * mm});
            skLineSegment(sketch, "E643", {"start": v(178.86, 357.26) * mm, "end": v(178.85, 357.81) * mm});
            skLineSegment(sketch, "E644", {"start": v(178.85, 357.81) * mm, "end": v(178.85, 360.58) * mm});
            skLineSegment(sketch, "E645", {"start": v(178.85, 360.58) * mm, "end": v(178.86, 361.14) * mm});
            skLineSegment(sketch, "E646", {"start": v(178.86, 361.14) * mm, "end": v(178.89, 361.66) * mm});
            skLineSegment(sketch, "E647", {"start": v(178.89, 361.66) * mm, "end": v(178.93, 362.16) * mm});
            skLineSegment(sketch, "E648", {"start": v(178.93, 362.16) * mm, "end": v(179, 362.62) * mm});
            skLineSegment(sketch, "E649", {"start": v(179, 362.62) * mm, "end": v(179.07, 363.05) * mm});
            skLineSegment(sketch, "E650", {"start": v(179.07, 363.05) * mm, "end": v(179.17, 363.46) * mm});
            skLineSegment(sketch, "E651", {"start": v(179.17, 363.46) * mm, "end": v(179.29, 363.83) * mm});
            skLineSegment(sketch, "E652", {"start": v(179.29, 363.83) * mm, "end": v(179.42, 364.18) * mm});
            skLineSegment(sketch, "E653", {"start": v(179.42, 364.18) * mm, "end": v(179.57, 364.49) * mm});
            skLineSegment(sketch, "E654", {"start": v(179.57, 364.49) * mm, "end": v(179.74, 364.77) * mm});
            skLineSegment(sketch, "E655", {"start": v(179.74, 364.77) * mm, "end": v(179.92, 365.03) * mm});
            skLineSegment(sketch, "E656", {"start": v(179.92, 365.03) * mm, "end": v(180.13, 365.25) * mm});
            skLineSegment(sketch, "E657", {"start": v(180.13, 365.25) * mm, "end": v(180.36, 365.45) * mm});
            skLineSegment(sketch, "E658", {"start": v(180.36, 365.45) * mm, "end": v(180.62, 365.63) * mm});
            skLineSegment(sketch, "E659", {"start": v(180.62, 365.63) * mm, "end": v(180.91, 365.8) * mm});
            skLineSegment(sketch, "E660", {"start": v(180.91, 365.8) * mm, "end": v(181.24, 365.94) * mm});
            skLineSegment(sketch, "E661", {"start": v(181.24, 365.94) * mm, "end": v(181.6, 366.07) * mm});
            skLineSegment(sketch, "E662", {"start": v(181.6, 366.07) * mm, "end": v(182, 366.19) * mm});
            skLineSegment(sketch, "E663", {"start": v(182, 366.19) * mm, "end": v(182.42, 366.28) * mm});
            skLineSegment(sketch, "E664", {"start": v(182.42, 366.28) * mm, "end": v(182.88, 366.36) * mm});
            skLineSegment(sketch, "E665", {"start": v(182.88, 366.36) * mm, "end": v(183.37, 366.42) * mm});
            skLineSegment(sketch, "E666", {"start": v(183.37, 366.42) * mm, "end": v(183.9, 366.47) * mm});
            skLineSegment(sketch, "E667", {"start": v(183.9, 366.47) * mm, "end": v(184.45, 366.5) * mm});
            skLineSegment(sketch, "E668", {"start": v(184.45, 366.5) * mm, "end": v(185.04, 366.5) * mm});
            skLineSegment(sketch, "E669", {"start": v(185.04, 366.5) * mm, "end": v(199.22, 366.5) * mm});
            skLineSegment(sketch, "E670", {"start": v(199.22, 366.5) * mm, "end": v(199.8, 366.5) * mm});
            skLineSegment(sketch, "E671", {"start": v(199.8, 366.5) * mm, "end": v(200.33, 366.47) * mm});
            skLineSegment(sketch, "E672", {"start": v(200.33, 366.47) * mm, "end": v(200.84, 366.42) * mm});
            skLineSegment(sketch, "E673", {"start": v(200.84, 366.42) * mm, "end": v(201.32, 366.37) * mm});
            skLineSegment(sketch, "E674", {"start": v(201.32, 366.37) * mm, "end": v(201.77, 366.29) * mm});
            skLineSegment(sketch, "E675", {"start": v(201.77, 366.29) * mm, "end": v(202.2, 366.2) * mm});
            skLineSegment(sketch, "E676", {"start": v(202.2, 366.2) * mm, "end": v(202.58, 366.09) * mm});
            skLineSegment(sketch, "E677", {"start": v(202.58, 366.09) * mm, "end": v(202.94, 365.96) * mm});
            skLineSegment(sketch, "E678", {"start": v(202.94, 365.96) * mm, "end": v(203.27, 365.82) * mm});
            skLineSegment(sketch, "E679", {"start": v(203.27, 365.82) * mm, "end": v(203.57, 365.66) * mm});
            skLineSegment(sketch, "E680", {"start": v(203.57, 365.66) * mm, "end": v(203.84, 365.48) * mm});
            skLineSegment(sketch, "E681", {"start": v(203.84, 365.48) * mm, "end": v(204.07, 365.29) * mm});
            skLineSegment(sketch, "E682", {"start": v(204.07, 365.29) * mm, "end": v(204.29, 365.07) * mm});
            skLineSegment(sketch, "E683", {"start": v(204.29, 365.07) * mm, "end": v(204.48, 364.83) * mm});
            skLineSegment(sketch, "E684", {"start": v(204.48, 364.83) * mm, "end": v(204.66, 364.56) * mm});
            skLineSegment(sketch, "E685", {"start": v(204.66, 364.56) * mm, "end": v(204.82, 364.27) * mm});
            skLineSegment(sketch, "E686", {"start": v(204.82, 364.27) * mm, "end": v(204.96, 363.95) * mm});
            skLineSegment(sketch, "E687", {"start": v(204.96, 363.95) * mm, "end": v(205.08, 363.61) * mm});
            skLineSegment(sketch, "E688", {"start": v(205.08, 363.61) * mm, "end": v(205.18, 363.24) * mm});
            skLineSegment(sketch, "E689", {"start": v(205.18, 363.24) * mm, "end": v(205.26, 362.84) * mm});
            skLineSegment(sketch, "E690", {"start": v(205.26, 362.84) * mm, "end": v(205.33, 362.42) * mm});
            skLineSegment(sketch, "E691", {"start": v(205.33, 362.42) * mm, "end": v(205.37, 361.98) * mm});
            skLineSegment(sketch, "E692", {"start": v(205.37, 361.98) * mm, "end": v(205.4, 361.5) * mm});
            skLineSegment(sketch, "E693", {"start": v(205.4, 361.5) * mm, "end": v(205.41, 361) * mm});
            skLineSegment(sketch, "E694", {"start": v(205.41, 361) * mm, "end": v(205.41, 360.49) * mm});
            skLineSegment(sketch, "E695", {"start": v(205.41, 360.49) * mm, "end": v(200.29, 359.27) * mm});
            skLineSegment(sketch, "E696", {"start": v(104.6, 362.17) * mm, "end": v(104.6, 341.5) * mm});
            skLineSegment(sketch, "E697", {"start": v(104.6, 341.5) * mm, "end": v(98.88, 341.5) * mm});
            skLineSegment(sketch, "E698", {"start": v(98.88, 341.5) * mm, "end": v(98.88, 366.5) * mm});
            skLineSegment(sketch, "E699", {"start": v(98.88, 366.5) * mm, "end": v(120.26, 366.5) * mm});
            skLineSegment(sketch, "E700", {"start": v(120.26, 366.5) * mm, "end": v(120.75, 366.5) * mm});
            skLineSegment(sketch, "E701", {"start": v(120.75, 366.5) * mm, "end": v(121.2, 366.47) * mm});
            skLineSegment(sketch, "E702", {"start": v(121.2, 366.47) * mm, "end": v(121.65, 366.43) * mm});
            skLineSegment(sketch, "E703", {"start": v(121.65, 366.43) * mm, "end": v(122.06, 366.37) * mm});
            skLineSegment(sketch, "E704", {"start": v(122.06, 366.37) * mm, "end": v(122.45, 366.3) * mm});
            skLineSegment(sketch, "E705", {"start": v(122.45, 366.3) * mm, "end": v(122.82, 366.21) * mm});
            skLineSegment(sketch, "E706", {"start": v(122.82, 366.21) * mm, "end": v(123.17, 366.1) * mm});
            skLineSegment(sketch, "E707", {"start": v(123.17, 366.1) * mm, "end": v(123.5, 365.99) * mm});
            skLineSegment(sketch, "E708", {"start": v(123.5, 365.99) * mm, "end": v(123.8, 365.85) * mm});
            skLineSegment(sketch, "E709", {"start": v(123.8, 365.85) * mm, "end": v(124.08, 365.7) * mm});
            skLineSegment(sketch, "E710", {"start": v(124.08, 365.7) * mm, "end": v(124.34, 365.53) * mm});
            skLineSegment(sketch, "E711", {"start": v(124.34, 365.53) * mm, "end": v(124.57, 365.35) * mm});
            skLineSegment(sketch, "E712", {"start": v(124.57, 365.35) * mm, "end": v(124.78, 365.15) * mm});
            skLineSegment(sketch, "E713", {"start": v(124.78, 365.15) * mm, "end": v(124.98, 364.93) * mm});
            skLineSegment(sketch, "E714", {"start": v(124.98, 364.93) * mm, "end": v(125.15, 364.69) * mm});
            skLineSegment(sketch, "E715", {"start": v(125.15, 364.69) * mm, "end": v(125.31, 364.43) * mm});
            skLineSegment(sketch, "E716", {"start": v(125.31, 364.43) * mm, "end": v(125.45, 364.15) * mm});
            skLineSegment(sketch, "E717", {"start": v(125.45, 364.15) * mm, "end": v(125.57, 363.85) * mm});
            skLineSegment(sketch, "E718", {"start": v(125.57, 363.85) * mm, "end": v(125.67, 363.53) * mm});
            skLineSegment(sketch, "E719", {"start": v(125.67, 363.53) * mm, "end": v(125.76, 363.2) * mm});
            skLineSegment(sketch, "E720", {"start": v(125.76, 363.2) * mm, "end": v(125.82, 362.84) * mm});
            skLineSegment(sketch, "E721", {"start": v(125.82, 362.84) * mm, "end": v(125.87, 362.46) * mm});
            skLineSegment(sketch, "E722", {"start": v(125.87, 362.46) * mm, "end": v(125.9, 362.06) * mm});
            skLineSegment(sketch, "E723", {"start": v(125.9, 362.06) * mm, "end": v(125.9, 361.65) * mm});
            skLineSegment(sketch, "E724", {"start": v(125.9, 361.65) * mm, "end": v(125.9, 355.8) * mm});
            skLineSegment(sketch, "E725", {"start": v(125.9, 355.8) * mm, "end": v(125.9, 355.4) * mm});
            skLineSegment(sketch, "E726", {"start": v(125.9, 355.4) * mm, "end": v(125.87, 355) * mm});
            skLineSegment(sketch, "E727", {"start": v(125.87, 355) * mm, "end": v(125.82, 354.63) * mm});
            skLineSegment(sketch, "E728", {"start": v(125.82, 354.63) * mm, "end": v(125.76, 354.28) * mm});
            skLineSegment(sketch, "E729", {"start": v(125.76, 354.28) * mm, "end": v(125.67, 353.94) * mm});
            skLineSegment(sketch, "E730", {"start": v(125.67, 353.94) * mm, "end": v(125.57, 353.62) * mm});
            skLineSegment(sketch, "E731", {"start": v(125.57, 353.62) * mm, "end": v(125.45, 353.32) * mm});
            skLineSegment(sketch, "E732", {"start": v(125.45, 353.32) * mm, "end": v(125.31, 353.05) * mm});
            skLineSegment(sketch, "E733", {"start": v(125.31, 353.05) * mm, "end": v(125.15, 352.79) * mm});
            skLineSegment(sketch, "E734", {"start": v(125.15, 352.79) * mm, "end": v(124.98, 352.54) * mm});
            skLineSegment(sketch, "E735", {"start": v(124.98, 352.54) * mm, "end": v(124.78, 352.32) * mm});
            skLineSegment(sketch, "E736", {"start": v(124.78, 352.32) * mm, "end": v(124.57, 352.12) * mm});
            skLineSegment(sketch, "E737", {"start": v(124.57, 352.12) * mm, "end": v(124.34, 351.93) * mm});
            skLineSegment(sketch, "E738", {"start": v(124.34, 351.93) * mm, "end": v(124.08, 351.76) * mm});
            skLineSegment(sketch, "E739", {"start": v(124.08, 351.76) * mm, "end": v(123.8, 351.6) * mm});
            skLineSegment(sketch, "E740", {"start": v(123.8, 351.6) * mm, "end": v(123.5, 351.47) * mm});
            skLineSegment(sketch, "E741", {"start": v(123.5, 351.47) * mm, "end": v(123.17, 351.35) * mm});
            skLineSegment(sketch, "E742", {"start": v(123.17, 351.35) * mm, "end": v(122.82, 351.25) * mm});
            skLineSegment(sketch, "E743", {"start": v(122.82, 351.25) * mm, "end": v(122.45, 351.16) * mm});
            skLineSegment(sketch, "E744", {"start": v(122.45, 351.16) * mm, "end": v(122.06, 351.08) * mm});
            skLineSegment(sketch, "E745", {"start": v(122.06, 351.08) * mm, "end": v(121.65, 351.03) * mm});
            skLineSegment(sketch, "E746", {"start": v(121.65, 351.03) * mm, "end": v(121.2, 350.99) * mm});
            skLineSegment(sketch, "E747", {"start": v(121.2, 350.99) * mm, "end": v(120.75, 350.96) * mm});
            skLineSegment(sketch, "E748", {"start": v(120.75, 350.96) * mm, "end": v(120.26, 350.96) * mm});
            skLineSegment(sketch, "E749", {"start": v(120.26, 350.96) * mm, "end": v(117, 350.96) * mm});
            skLineSegment(sketch, "E750", {"start": v(117, 350.96) * mm, "end": v(128.53, 341.5) * mm});
            skLineSegment(sketch, "E751", {"start": v(128.53, 341.5) * mm, "end": v(120.19, 341.5) * mm});
            skLineSegment(sketch, "E752", {"start": v(120.19, 341.5) * mm, "end": v(110.11, 350.96) * mm});
            skLineSegment(sketch, "E753", {"start": v(110.11, 355.24) * mm, "end": v(117.69, 355.24) * mm});
            skLineSegment(sketch, "E754", {"start": v(117.69, 355.24) * mm, "end": v(117.93, 355.24) * mm});
            skLineSegment(sketch, "E755", {"start": v(117.93, 355.24) * mm, "end": v(118.16, 355.25) * mm});
            skLineSegment(sketch, "E756", {"start": v(118.16, 355.25) * mm, "end": v(118.38, 355.26) * mm});
            skLineSegment(sketch, "E757", {"start": v(118.38, 355.26) * mm, "end": v(118.59, 355.29) * mm});
            skLineSegment(sketch, "E758", {"start": v(118.59, 355.29) * mm, "end": v(118.78, 355.31) * mm});
            skLineSegment(sketch, "E759", {"start": v(118.78, 355.31) * mm, "end": v(118.96, 355.35) * mm});
            skLineSegment(sketch, "E760", {"start": v(118.96, 355.35) * mm, "end": v(119.13, 355.39) * mm});
            skLineSegment(sketch, "E761", {"start": v(119.13, 355.39) * mm, "end": v(119.28, 355.43) * mm});
            skLineSegment(sketch, "E762", {"start": v(119.28, 355.43) * mm, "end": v(119.42, 355.48) * mm});
            skLineSegment(sketch, "E763", {"start": v(119.42, 355.48) * mm, "end": v(119.54, 355.54) * mm});
            skLineSegment(sketch, "E764", {"start": v(119.54, 355.54) * mm, "end": v(119.66, 355.6) * mm});
            skLineSegment(sketch, "E765", {"start": v(119.66, 355.6) * mm, "end": v(119.75, 355.67) * mm});
            skLineSegment(sketch, "E766", {"start": v(119.75, 355.67) * mm, "end": v(119.84, 355.75) * mm});
            skLineSegment(sketch, "E767", {"start": v(119.84, 355.75) * mm, "end": v(119.93, 355.83) * mm});
            skLineSegment(sketch, "E768", {"start": v(119.93, 355.83) * mm, "end": v(120, 355.93) * mm});
            skLineSegment(sketch, "E769", {"start": v(120, 355.93) * mm, "end": v(120.06, 356.04) * mm});
            skLineSegment(sketch, "E770", {"start": v(120.06, 356.04) * mm, "end": v(120.12, 356.15) * mm});
            skLineSegment(sketch, "E771", {"start": v(120.12, 356.15) * mm, "end": v(120.17, 356.27) * mm});
            skLineSegment(sketch, "E772", {"start": v(120.17, 356.27) * mm, "end": v(120.22, 356.4) * mm});
            skLineSegment(sketch, "E773", {"start": v(120.22, 356.4) * mm, "end": v(120.25, 356.55) * mm});
            skLineSegment(sketch, "E774", {"start": v(120.25, 356.55) * mm, "end": v(120.28, 356.7) * mm});
            skLineSegment(sketch, "E775", {"start": v(120.28, 356.7) * mm, "end": v(120.3, 356.87) * mm});
            skLineSegment(sketch, "E776", {"start": v(120.3, 356.87) * mm, "end": v(120.3, 357.04) * mm});
            skLineSegment(sketch, "E777", {"start": v(120.3, 357.04) * mm, "end": v(120.31, 357.22) * mm});
            skLineSegment(sketch, "E778", {"start": v(120.31, 357.22) * mm, "end": v(120.31, 360.21) * mm});
            skLineSegment(sketch, "E779", {"start": v(120.31, 360.21) * mm, "end": v(120.3, 360.39) * mm});
            skLineSegment(sketch, "E780", {"start": v(120.3, 360.39) * mm, "end": v(120.3, 360.56) * mm});
            skLineSegment(sketch, "E781", {"start": v(120.3, 360.56) * mm, "end": v(120.28, 360.72) * mm});
            skLineSegment(sketch, "E782", {"start": v(120.28, 360.72) * mm, "end": v(120.25, 360.87) * mm});
            skLineSegment(sketch, "E783", {"start": v(120.25, 360.87) * mm, "end": v(120.22, 361) * mm});
            skLineSegment(sketch, "E784", {"start": v(120.22, 361) * mm, "end": v(120.17, 361.14) * mm});
            skLineSegment(sketch, "E785", {"start": v(120.17, 361.14) * mm, "end": v(120.12, 361.26) * mm});
            skLineSegment(sketch, "E786", {"start": v(120.12, 361.26) * mm, "end": v(120.06, 361.37) * mm});
            skLineSegment(sketch, "E787", {"start": v(120.06, 361.37) * mm, "end": v(120, 361.48) * mm});
            skLineSegment(sketch, "E788", {"start": v(120, 361.48) * mm, "end": v(119.93, 361.57) * mm});
            skLineSegment(sketch, "E789", {"start": v(119.93, 361.57) * mm, "end": v(119.84, 361.66) * mm});
            skLineSegment(sketch, "E790", {"start": v(119.84, 361.66) * mm, "end": v(119.75, 361.74) * mm});
            skLineSegment(sketch, "E791", {"start": v(119.75, 361.74) * mm, "end": v(119.66, 361.8) * mm});
            skLineSegment(sketch, "E792", {"start": v(119.66, 361.8) * mm, "end": v(119.54, 361.87) * mm});
            skLineSegment(sketch, "E793", {"start": v(119.54, 361.87) * mm, "end": v(119.42, 361.92) * mm});
            skLineSegment(sketch, "E794", {"start": v(119.42, 361.92) * mm, "end": v(119.28, 361.98) * mm});
            skLineSegment(sketch, "E795", {"start": v(119.28, 361.98) * mm, "end": v(119.13, 362.02) * mm});
            skLineSegment(sketch, "E796", {"start": v(119.13, 362.02) * mm, "end": v(118.96, 362.06) * mm});
            skLineSegment(sketch, "E797", {"start": v(118.96, 362.06) * mm, "end": v(118.78, 362.1) * mm});
            skLineSegment(sketch, "E798", {"start": v(118.78, 362.1) * mm, "end": v(118.59, 362.12) * mm});
            skLineSegment(sketch, "E799", {"start": v(118.59, 362.12) * mm, "end": v(118.38, 362.14) * mm});
            skLineSegment(sketch, "E800", {"start": v(118.38, 362.14) * mm, "end": v(118.16, 362.16) * mm});
            skLineSegment(sketch, "E801", {"start": v(118.16, 362.16) * mm, "end": v(117.93, 362.17) * mm});
            skLineSegment(sketch, "E802", {"start": v(117.93, 362.17) * mm, "end": v(117.69, 362.17) * mm});
            skLineSegment(sketch, "E803", {"start": v(117.69, 362.17) * mm, "end": v(104.6, 362.17) * mm});
            skLineSegment(sketch, "E804", {"start": v(235.19, 351.48) * mm, "end": v(229.8, 361.65) * mm});
            skLineSegment(sketch, "E805", {"start": v(229.8, 361.65) * mm, "end": v(224.25, 351.48) * mm});
            skLineSegment(sketch, "E806", {"start": v(221.75, 346.97) * mm, "end": v(218.85, 341.5) * mm});
            skLineSegment(sketch, "E807", {"start": v(218.85, 341.5) * mm, "end": v(213.06, 341.5) * mm});
            skLineSegment(sketch, "E808", {"start": v(213.06, 341.5) * mm, "end": v(227.2, 366.5) * mm});
            skLineSegment(sketch, "E809", {"start": v(227.2, 366.5) * mm, "end": v(232.79, 366.5) * mm});
            skLineSegment(sketch, "E810", {"start": v(232.79, 366.5) * mm, "end": v(247.12, 341.5) * mm});
            skLineSegment(sketch, "E811", {"start": v(247.12, 341.5) * mm, "end": v(240.58, 341.5) * mm});
            skLineSegment(sketch, "E812", {"start": v(240.58, 341.5) * mm, "end": v(237.59, 346.97) * mm});
            skLineSegment(sketch, "E813", {"start": v(237.59, 346.97) * mm, "end": v(229.8, 346.97) * mm});
            skLineSegment(sketch, "E814", {"start": v(229.8, 351.48) * mm, "end": v(235.19, 351.48) * mm});
            skLineSegment(sketch, "E815", {"start": v(273.9, 358.5) * mm, "end": v(279.72, 358.5) * mm});
            skLineSegment(sketch, "E816", {"start": v(71.25, 351.25) * mm, "end": v(71.25, 355.56) * mm});
            skLineSegment(sketch, "E817", {"start": v(279.72, 361.5) * mm, "end": v(273.9, 361.5) * mm});
            skLineSegment(sketch, "E818", {"start": v(110.11, 350.96) * mm, "end": v(110.11, 355.24) * mm});
            skLineSegment(sketch, "E819", {"start": v(224.25, 351.48) * mm, "end": v(221.75, 346.97) * mm});
            skLineSegment(sketch, "E820", {"start": v(229.8, 346.97) * mm, "end": v(229.8, 351.48) * mm});
            skLineSegment(sketch, "E821", {"start": v(316.75, 359.35) * mm, "end": v(316.74, 358.99) * mm});
            skLineSegment(sketch, "E822", {"start": v(316.74, 358.99) * mm, "end": v(316.72, 358.64) * mm});
            skLineSegment(sketch, "E823", {"start": v(316.72, 358.64) * mm, "end": v(316.68, 358.32) * mm});
            skLineSegment(sketch, "E824", {"start": v(316.68, 358.32) * mm, "end": v(316.63, 358) * mm});
            skLineSegment(sketch, "E825", {"start": v(316.63, 358) * mm, "end": v(316.56, 357.7) * mm});
            skLineSegment(sketch, "E826", {"start": v(316.56, 357.7) * mm, "end": v(316.48, 357.43) * mm});
            skLineSegment(sketch, "E827", {"start": v(316.48, 357.43) * mm, "end": v(316.39, 357.16) * mm});
            skLineSegment(sketch, "E828", {"start": v(316.39, 357.16) * mm, "end": v(316.27, 356.92) * mm});
            skLineSegment(sketch, "E829", {"start": v(316.27, 356.92) * mm, "end": v(316.15, 356.68) * mm});
            skLineSegment(sketch, "E830", {"start": v(316.15, 356.68) * mm, "end": v(316, 356.47) * mm});
            skLineSegment(sketch, "E831", {"start": v(316, 356.47) * mm, "end": v(315.85, 356.26) * mm});
            skLineSegment(sketch, "E832", {"start": v(315.85, 356.26) * mm, "end": v(315.68, 356.08) * mm});
            skLineSegment(sketch, "E833", {"start": v(315.68, 356.08) * mm, "end": v(315.5, 355.9) * mm});
            skLineSegment(sketch, "E834", {"start": v(315.5, 355.9) * mm, "end": v(315.28, 355.74) * mm});
            skLineSegment(sketch, "E835", {"start": v(315.28, 355.74) * mm, "end": v(315.05, 355.59) * mm});
            skLineSegment(sketch, "E836", {"start": v(315.05, 355.59) * mm, "end": v(314.8, 355.44) * mm});
            skLineSegment(sketch, "E837", {"start": v(314.8, 355.44) * mm, "end": v(314.51, 355.3) * mm});
            skLineSegment(sketch, "E838", {"start": v(314.51, 355.3) * mm, "end": v(314.21, 355.18) * mm});
            skLineSegment(sketch, "E839", {"start": v(314.21, 355.18) * mm, "end": v(313.74, 355) * mm});
            skLineSegment(sketch, "E840", {"start": v(313.74, 354.3) * mm, "end": v(314.14, 354.19) * mm});
            skLineSegment(sketch, "E841", {"start": v(314.14, 354.19) * mm, "end": v(314.52, 354.06) * mm});
            skLineSegment(sketch, "E842", {"start": v(314.52, 354.06) * mm, "end": v(314.87, 353.93) * mm});
            skLineSegment(sketch, "E843", {"start": v(314.87, 353.93) * mm, "end": v(315.2, 353.79) * mm});
            skLineSegment(sketch, "E844", {"start": v(315.2, 353.79) * mm, "end": v(315.52, 353.63) * mm});
            skLineSegment(sketch, "E845", {"start": v(315.52, 353.63) * mm, "end": v(315.8, 353.45) * mm});
            skLineSegment(sketch, "E846", {"start": v(315.8, 353.45) * mm, "end": v(316.07, 353.27) * mm});
            skLineSegment(sketch, "E847", {"start": v(316.07, 353.27) * mm, "end": v(316.31, 353.07) * mm});
            skLineSegment(sketch, "E848", {"start": v(316.31, 353.07) * mm, "end": v(316.54, 352.86) * mm});
            skLineSegment(sketch, "E849", {"start": v(316.54, 352.86) * mm, "end": v(316.74, 352.63) * mm});
            skLineSegment(sketch, "E850", {"start": v(316.74, 352.63) * mm, "end": v(316.93, 352.39) * mm});
            skLineSegment(sketch, "E851", {"start": v(316.93, 352.39) * mm, "end": v(317.1, 352.13) * mm});
            skLineSegment(sketch, "E852", {"start": v(317.1, 352.13) * mm, "end": v(317.24, 351.86) * mm});
            skLineSegment(sketch, "E853", {"start": v(317.24, 351.86) * mm, "end": v(317.36, 351.56) * mm});
            skLineSegment(sketch, "E854", {"start": v(317.36, 351.56) * mm, "end": v(317.47, 351.26) * mm});
            skLineSegment(sketch, "E855", {"start": v(317.47, 351.26) * mm, "end": v(317.56, 350.94) * mm});
            skLineSegment(sketch, "E856", {"start": v(317.56, 350.94) * mm, "end": v(317.63, 350.6) * mm});
            skLineSegment(sketch, "E857", {"start": v(317.63, 350.6) * mm, "end": v(317.67, 350.25) * mm});
            skLineSegment(sketch, "E858", {"start": v(317.67, 350.25) * mm, "end": v(317.7, 349.88) * mm});
            skLineSegment(sketch, "E859", {"start": v(317.7, 349.88) * mm, "end": v(317.71, 349.5) * mm});
            skArc(sketch, "E860", {"start": v(313.74, 355) * mm, "mid": v(313.49, 354.65) * mm, "end": v(313.74, 354.3) * mm});
            skLineSegment(sketch, "E861", {"start": v(305, 44) * mm, "end": v(285, 44) * mm});
            skLineSegment(sketch, "E862", {"start": v(60, 59) * mm, "end": v(75, 44) * mm});
            skLineSegment(sketch, "E863", {"start": v(75, 44) * mm, "end": v(95, 44) * mm});
            skPoint(sketch, "E864", {"position": v(5, 4) * mm});
            skSolve(sketch);
        }
        {
            var Q0;
            Q0=makeQuery(id+"F0.imprint","IMPRINT",FACE,{"disambiguationData":[TD([[makeQuery(id+"F0.imprint","IMPRINT",EDGE,{"derivedFrom":sQuery(id+"F0.wireOp",EDGE,"E0")}),1.0]])]});
            var Q1;
            Q1=makeQuery(id+"F0.imprint","IMPRINT",FACE,{"disambiguationData":[TD([[makeQuery(id+"F0.imprint","IMPRINT",EDGE,{"derivedFrom":sQuery(id+"F0.wireOp",EDGE,"E64")}),1.0]])]});
            extrude(context, id + "F1", {"entities" : qUnion([Q0, Q1]), "depth" : 25 * mm, "offsetDistance" : 25 * mm});
        }
    });
